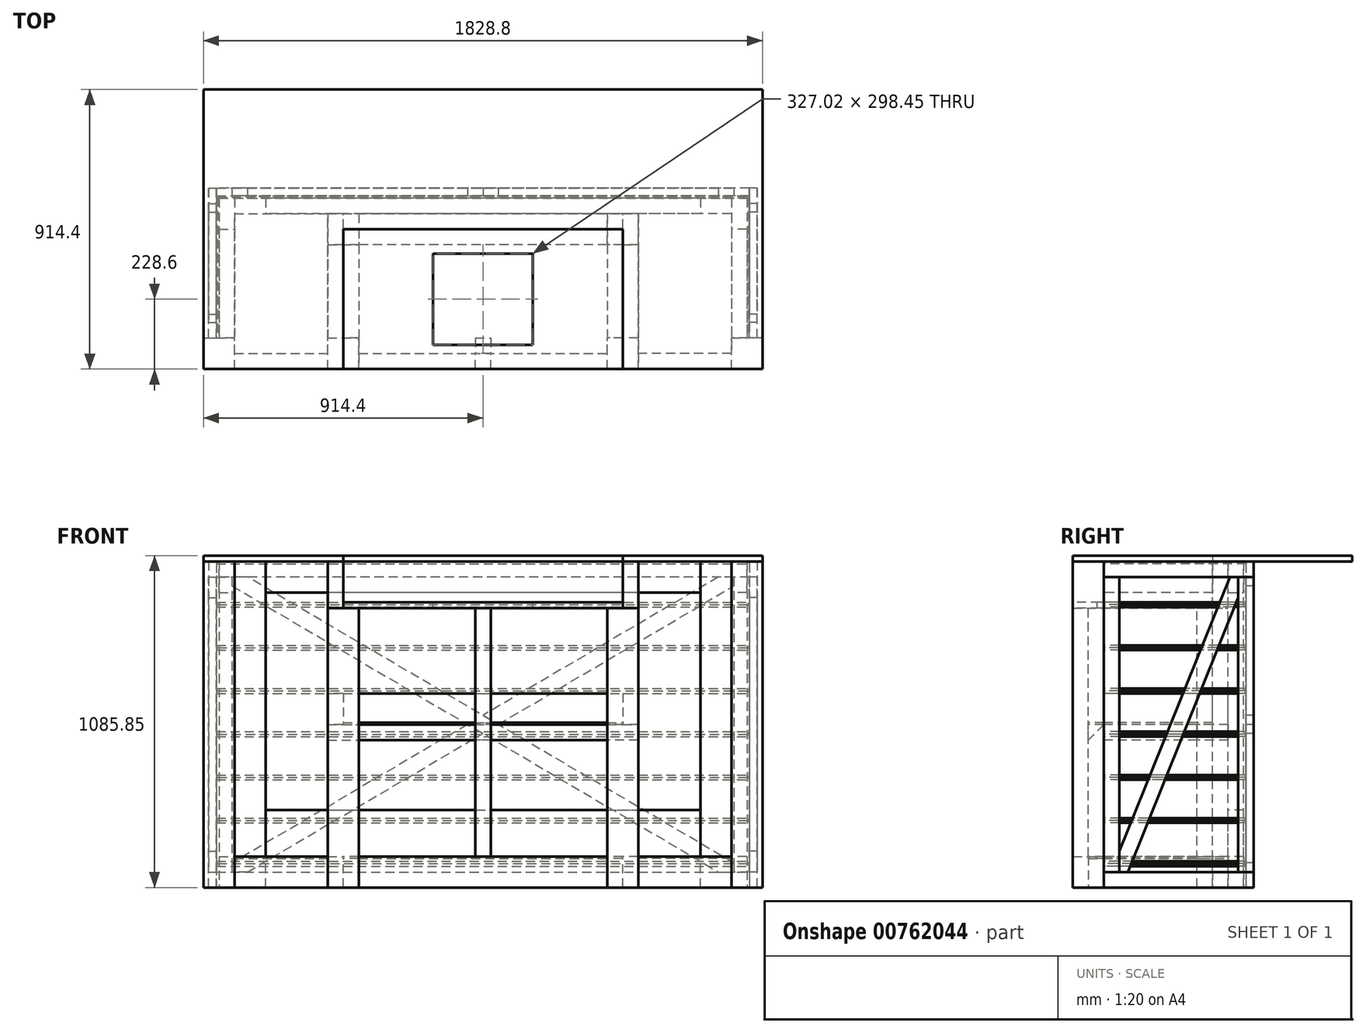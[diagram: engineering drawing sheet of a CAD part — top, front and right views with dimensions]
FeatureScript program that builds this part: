
annotation { "Feature Type Name" : "Feature", "Feature Type Description" : "" }
export const myFeature = defineFeature(function(context is Context, id is Id, definition is map)
    precondition{}
    {
        {
            var Q0;
            Q0=qCreatedBy(makeId("Top.planeOp"),FACE);
            var sketch = newSketch(context, id + "F0", { "sketchPlane" : qUnion([Q0])});
            skLineSegment(sketch, "E0.bottom", {"start": v(-914.4, -457.2) * mm, "end": v(-457.2, -457.2) * mm});
            skLineSegment(sketch, "E0.top", {"start": v(-914.4, 457.2) * mm, "end": v(914.4, 457.2) * mm});
            skLineSegment(sketch, "E0.left", {"start": v(-914.4, -457.2) * mm, "end": v(-914.4, 457.2) * mm});
            skLineSegment(sketch, "E0.right", {"start": v(914.4, -457.2) * mm, "end": v(914.4, 457.2) * mm});
            skLineSegment(sketch, "E1", {"start": v(0, 457.2) * mm, "end": v(0, -457.2) * mm, "construction": true});
            skLineSegment(sketch, "E2", {"start": v(914.4, 0) * mm, "end": v(-914.4, 0) * mm, "construction": true});
            skLineSegment(sketch, "E3.top", {"start": v(-457.2, 0) * mm, "end": v(457.2, 0) * mm});
            skLineSegment(sketch, "E3.left", {"start": v(-457.2, -457.2) * mm, "end": v(-457.2, 0) * mm});
            skLineSegment(sketch, "E3.right", {"start": v(457.2, -457.2) * mm, "end": v(457.2, 0) * mm});
            skLineSegment(sketch, "E4.trimOffspring", {"start": v(457.2, -457.2) * mm, "end": v(914.4, -457.2) * mm});
            skSolve(sketch);
        }
        {
            var Q0;
            Q0 = qSketchRegion(id + "F0", true);
            extrude(context, id + "F1", {"entities" : qUnion([Q0]), "depth" : 19.05 * mm, "offsetDistance" : 25.4 * mm});
        }
        {
            var Q0;
            Q0=makeQuery(id+"F1.opExtrude","CAP_FACE",FACE,{"disambiguationData":[OSD([sQuery(id+"F0.wireOp",EDGE,"E0.bottom"),sQuery(id+"F0.wireOp",EDGE,"E0.top"),sQuery(id+"F0.wireOp",EDGE,"E0.left"),sQuery(id+"F0.wireOp",EDGE,"E0.right"),sQuery(id+"F0.wireOp",EDGE,"E3.top"),sQuery(id+"F0.wireOp",EDGE,"E3.left"),sQuery(id+"F0.wireOp",EDGE,"E3.right"),sQuery(id+"F0.wireOp",EDGE,"E4.trimOffspring")])],"isStart":true});
            var sketch = newSketch(context, id + "F2", { "sketchPlane" : qUnion([Q0])});
            skLineSegment(sketch, "E5.bottom", {"start": v(-457.2, 0) * mm, "end": v(457.2, 0) * mm});
            skLineSegment(sketch, "E5.top", {"start": v(-457.2, -50.8) * mm, "end": v(457.2, -50.8) * mm});
            skLineSegment(sketch, "E5.left", {"start": v(-457.2, 0) * mm, "end": v(-457.2, -50.8) * mm});
            skLineSegment(sketch, "E5.right", {"start": v(457.2, 0) * mm, "end": v(457.2, -50.8) * mm});
            skSolve(sketch);
        }
        {
            var Q0;
            Q0 = qSketchRegion(id + "F2", true);
            extrude(context, id + "F3", {"entities" : qUnion([Q0]), "depth" : 152.4 * mm, "offsetDistance" : 25.4 * mm});
        }
        {
            var Q0;
            Q0=makeQuery(id+"F1.opExtrude","CAP_FACE",FACE,{"disambiguationData":[OSD([sQuery(id+"F0.wireOp",EDGE,"E0.bottom"),sQuery(id+"F0.wireOp",EDGE,"E0.top"),sQuery(id+"F0.wireOp",EDGE,"E0.left"),sQuery(id+"F0.wireOp",EDGE,"E0.right"),sQuery(id+"F0.wireOp",EDGE,"E3.top"),sQuery(id+"F0.wireOp",EDGE,"E3.left"),sQuery(id+"F0.wireOp",EDGE,"E3.right"),sQuery(id+"F0.wireOp",EDGE,"E4.trimOffspring")])],"isStart":true});
            var sketch = newSketch(context, id + "F4", { "sketchPlane" : qUnion([Q0])});
            skLineSegment(sketch, "E6.bottom", {"start": v(-914.4, 457.2) * mm, "end": v(-812.8, 457.2) * mm});
            skLineSegment(sketch, "E6.top", {"start": v(-914.4, 355.6) * mm, "end": v(-812.8, 355.6) * mm});
            skLineSegment(sketch, "E6.left", {"start": v(-914.4, 457.2) * mm, "end": v(-914.4, 355.6) * mm});
            skLineSegment(sketch, "E6.right", {"start": v(-812.8, 457.2) * mm, "end": v(-812.8, 355.6) * mm});
            skLineSegment(sketch, "E7", {"start": v(0, 0) * mm, "end": v(0, 457.2) * mm, "construction": true});
            skLineSegment(sketch, "E8.MirrorCS", {"start": v(914.4, 457.2) * mm, "end": v(812.8, 457.2) * mm});
            skLineSegment(sketch, "E9.MirrorCS", {"start": v(914.4, 355.6) * mm, "end": v(812.8, 355.6) * mm});
            skLineSegment(sketch, "E10.MirrorCS", {"start": v(812.8, 457.2) * mm, "end": v(812.8, 355.6) * mm});
            skLineSegment(sketch, "E11.MirrorCS", {"start": v(914.4, 457.2) * mm, "end": v(914.4, 355.6) * mm});
            skSolve(sketch);
        }
        {
            var Q0;
            Q0 = qSketchRegion(id + "F4", true);
            extrude(context, id + "F5", {"entities" : qUnion([Q0]), "depth" : 1066.8 * mm, "offsetDistance" : 25.4 * mm});
        }
        {
            var Q0;
            Q0=makeQuery(id+"F1.opExtrude","CAP_FACE",FACE,{"disambiguationData":[OSD([sQuery(id+"F0.wireOp",EDGE,"E0.bottom"),sQuery(id+"F0.wireOp",EDGE,"E0.top"),sQuery(id+"F0.wireOp",EDGE,"E0.left"),sQuery(id+"F0.wireOp",EDGE,"E0.right"),sQuery(id+"F0.wireOp",EDGE,"E3.top"),sQuery(id+"F0.wireOp",EDGE,"E3.left"),sQuery(id+"F0.wireOp",EDGE,"E3.right"),sQuery(id+"F0.wireOp",EDGE,"E4.trimOffspring")])],"isStart":true});
            var sketch = newSketch(context, id + "F6", { "sketchPlane" : qUnion([Q0])});
            skLineSegment(sketch, "E12.bottom", {"start": v(-457.2, 457.2) * mm, "end": v(-508, 457.2) * mm});
            skLineSegment(sketch, "E12.top", {"start": v(-457.2, -50.8) * mm, "end": v(-508, -50.8) * mm});
            skLineSegment(sketch, "E12.left", {"start": v(-457.2, 457.2) * mm, "end": v(-457.2, -50.8) * mm});
            skLineSegment(sketch, "E12.right", {"start": v(-508, 457.2) * mm, "end": v(-508, -50.8) * mm});
            skLineSegment(sketch, "E13", {"start": v(0, 0) * mm, "end": v(0, 457.2) * mm, "construction": true});
            skLineSegment(sketch, "E14.MirrorCS", {"start": v(457.2, 457.2) * mm, "end": v(508, 457.2) * mm});
            skLineSegment(sketch, "E15.MirrorCS", {"start": v(457.2, -50.8) * mm, "end": v(508, -50.8) * mm});
            skLineSegment(sketch, "E16.MirrorCS", {"start": v(457.2, 457.2) * mm, "end": v(457.2, -50.8) * mm});
            skLineSegment(sketch, "E17.MirrorCS", {"start": v(508, 457.2) * mm, "end": v(508, -50.8) * mm});
            skSolve(sketch);
        }
        {
            var Q0;
            Q0 = qSketchRegion(id + "F6", true);
            extrude(context, id + "F7", {"entities" : qUnion([Q0]), "depth" : 152.4 * mm, "offsetDistance" : 25.4 * mm});
        }
        {
            var Q0;
            Q0=makeQuery(id+"F3.opExtrude","CAP_FACE",FACE,{"disambiguationData":[OSD([sQuery(id+"F2.wireOp",EDGE,"E5.bottom"),sQuery(id+"F2.wireOp",EDGE,"E5.top"),sQuery(id+"F2.wireOp",EDGE,"E5.left"),sQuery(id+"F2.wireOp",EDGE,"E5.right")])],"isStart":false});
            var sketch = newSketch(context, id + "F8", { "sketchPlane" : qUnion([Q0])});
            skLineSegment(sketch, "E18.bottom", {"start": v(-457.2, 0) * mm, "end": v(457.2, 0) * mm});
            skLineSegment(sketch, "E18.top", {"start": v(-457.2, 457.2) * mm, "end": v(457.2, 457.2) * mm});
            skLineSegment(sketch, "E18.left", {"start": v(-457.2, 0) * mm, "end": v(-457.2, 457.2) * mm});
            skLineSegment(sketch, "E18.right", {"start": v(457.2, 0) * mm, "end": v(457.2, 457.2) * mm});
            skSolve(sketch);
        }
        {
            var Q0;
            Q0 = qSketchRegion(id + "F8", true);
            extrude(context, id + "F9", {"entities" : qUnion([Q0]), "oppositeDirection" : true, "depth" : 19.05 * mm, "offsetDistance" : 25.4 * mm});
        }
        {
            var Q0;
            Q0=makeQuery(id+"F9.opExtrude","CAP_FACE",FACE,{"disambiguationData":[OSD([sQuery(id+"F8.wireOp",EDGE,"E18.bottom"),sQuery(id+"F8.wireOp",EDGE,"E18.top"),sQuery(id+"F8.wireOp",EDGE,"E18.left"),sQuery(id+"F8.wireOp",EDGE,"E18.right")])],"isStart":false});
            var sketch = newSketch(context, id + "F10", { "sketchPlane" : qUnion([Q0])});
            skLineSegment(sketch, "E19", {"start": v(0, 0) * mm, "end": v(0, -457.2) * mm, "construction": true});
            skLineSegment(sketch, "E20.bottom", {"start": v(163.51, -79.37) * mm, "end": v(-163.51, -79.37) * mm});
            skLineSegment(sketch, "E20.top", {"start": v(163.51, -377.82) * mm, "end": v(-163.51, -377.82) * mm});
            skLineSegment(sketch, "E20.left", {"start": v(163.51, -79.37) * mm, "end": v(163.51, -377.82) * mm});
            skLineSegment(sketch, "E20.right", {"start": v(-163.51, -79.37) * mm, "end": v(-163.51, -377.82) * mm});
            skPoint(sketch, "E20.middle", {"position": v(0, -228.6) * mm});
            skSolve(sketch);
        }
        {
            var Q0;
            Q0=makeQuery(id+"F10.imprint","IMPRINT",FACE,{"disambiguationData":[TD([[makeQuery(id+"F10.imprint","IMPRINT",EDGE,{"derivedFrom":sQuery(id+"F10.wireOp",EDGE,"E20.bottom")}),1.0]])]});
            extrude(context, id + "F11", {"entities" : qUnion([Q0]), "operationType" : NewBodyOperationType.REMOVE, "endBound" : BoundingType.UP_TO_NEXT, "oppositeDirection" : true, "depth" : 34.92 * mm, "offsetDistance" : 25.4 * mm});
        }
        {
            var Q0;
            Q0=makeQuery(id+"F7.opExtrude","CAP_FACE",FACE,{"disambiguationData":[OSD([sQuery(id+"F6.wireOp",EDGE,"E12.bottom"),sQuery(id+"F6.wireOp",EDGE,"E12.top"),sQuery(id+"F6.wireOp",EDGE,"E12.left"),sQuery(id+"F6.wireOp",EDGE,"E12.right")])],"isStart":false});
            var sketch = newSketch(context, id + "F12", { "sketchPlane" : qUnion([Q0])});
            skLineSegment(sketch, "E21.bottom", {"start": v(-508, 457.2) * mm, "end": v(-406.4, 457.2) * mm});
            skLineSegment(sketch, "E21.top", {"start": v(-508, 355.6) * mm, "end": v(-406.4, 355.6) * mm});
            skLineSegment(sketch, "E21.left", {"start": v(-508, 457.2) * mm, "end": v(-508, 355.6) * mm});
            skLineSegment(sketch, "E21.right", {"start": v(-406.4, 457.2) * mm, "end": v(-406.4, 355.6) * mm});
            skLineSegment(sketch, "E22", {"start": v(0, 0) * mm, "end": v(0, 457.2) * mm, "construction": true});
            skLineSegment(sketch, "E23.MirrorCS", {"start": v(508, 457.2) * mm, "end": v(406.4, 457.2) * mm});
            skLineSegment(sketch, "E24.MirrorCS", {"start": v(508, 355.6) * mm, "end": v(406.4, 355.6) * mm});
            skLineSegment(sketch, "E25.MirrorCS", {"start": v(406.4, 457.2) * mm, "end": v(406.4, 355.6) * mm});
            skLineSegment(sketch, "E26.MirrorCS", {"start": v(508, 457.2) * mm, "end": v(508, 355.6) * mm});
            skSolve(sketch);
        }
        {
            var Q0;
            Q0 = qSketchRegion(id + "F12", true);
            var Q1;
            Q1=makeQuery(id+"F5.opExtrude","CAP_FACE",FACE,{"disambiguationData":[OSD([sQuery(id+"F4.wireOp",EDGE,"E6.bottom"),sQuery(id+"F4.wireOp",EDGE,"E6.top"),sQuery(id+"F4.wireOp",EDGE,"E6.left"),sQuery(id+"F4.wireOp",EDGE,"E6.right")])],"isStart":false});
            extrude(context, id + "F13", {"entities" : qUnion([Q0]), "endBound" : BoundingType.UP_TO_SURFACE, "depth" : 25.4 * mm, "endBoundEntityFace" : qUnion([Q1]), "offsetDistance" : 25.4 * mm});
        }
        {
            var Q0;
            Q0=makeQuery(id+"F9.opExtrude","CAP_FACE",FACE,{"disambiguationData":[OSD([sQuery(id+"F8.wireOp",EDGE,"E18.bottom"),sQuery(id+"F8.wireOp",EDGE,"E18.top"),sQuery(id+"F8.wireOp",EDGE,"E18.left"),sQuery(id+"F8.wireOp",EDGE,"E18.right")])],"isStart":true});
            var sketch = newSketch(context, id + "F14", { "sketchPlane" : qUnion([Q0])});
            skLineSegment(sketch, "E27", {"start": v(0, 0) * mm, "end": v(0, 457.2) * mm, "construction": true});
            skLineSegment(sketch, "E28.bottom", {"start": v(25.4, 457.2) * mm, "end": v(-25.4, 457.2) * mm});
            skLineSegment(sketch, "E28.top", {"start": v(25.4, 406.4) * mm, "end": v(-25.4, 406.4) * mm});
            skLineSegment(sketch, "E28.left", {"start": v(25.4, 457.2) * mm, "end": v(25.4, 406.4) * mm});
            skLineSegment(sketch, "E28.right", {"start": v(-25.4, 457.2) * mm, "end": v(-25.4, 406.4) * mm});
            skSolve(sketch);
        }
        {
            var Q0;
            Q0 = qSketchRegion(id + "F14", true);
            var Q1;
            Q1=makeQuery(id+"F13.opExtrude","CAP_FACE",FACE,{"disambiguationData":[OSD([sQuery(id+"F12.wireOp",EDGE,"E21.bottom"),sQuery(id+"F12.wireOp",EDGE,"E21.top"),sQuery(id+"F12.wireOp",EDGE,"E21.left"),sQuery(id+"F12.wireOp",EDGE,"E21.right")])],"isStart":false});
            extrude(context, id + "F15", {"entities" : qUnion([Q0]), "depth" : 812.8 * mm, "endBoundEntityFace" : qUnion([Q1]), "offsetDistance" : 25.4 * mm});
        }
        {
            var Q0;
            Q0=makeQuery(id+"F7.opExtrude","CAP_FACE",FACE,{"disambiguationData":[OSD([sQuery(id+"F6.wireOp",EDGE,"E14.MirrorCS"),sQuery(id+"F6.wireOp",EDGE,"E15.MirrorCS"),sQuery(id+"F6.wireOp",EDGE,"E16.MirrorCS"),sQuery(id+"F6.wireOp",EDGE,"E17.MirrorCS")])],"isStart":false});
            var sketch = newSketch(context, id + "F16", { "sketchPlane" : qUnion([Q0])});
            skLineSegment(sketch, "E29.bottom", {"start": v(508, -50.8) * mm, "end": v(406.4, -50.8) * mm});
            skLineSegment(sketch, "E29.top", {"start": v(508, 50.8) * mm, "end": v(406.4, 50.8) * mm});
            skLineSegment(sketch, "E29.left", {"start": v(508, -50.8) * mm, "end": v(508, 50.8) * mm});
            skLineSegment(sketch, "E29.right", {"start": v(406.4, -50.8) * mm, "end": v(406.4, 50.8) * mm});
            skLineSegment(sketch, "E30", {"start": v(0, 0) * mm, "end": v(0, 457.2) * mm, "construction": true});
            skLineSegment(sketch, "E31.MirrorCS", {"start": v(-508, -50.8) * mm, "end": v(-406.4, -50.8) * mm});
            skLineSegment(sketch, "E32.MirrorCS", {"start": v(-508, 50.8) * mm, "end": v(-406.4, 50.8) * mm});
            skLineSegment(sketch, "E33.MirrorCS", {"start": v(-406.4, -50.8) * mm, "end": v(-406.4, 50.8) * mm});
            skLineSegment(sketch, "E34.MirrorCS", {"start": v(-508, -50.8) * mm, "end": v(-508, 50.8) * mm});
            skSolve(sketch);
        }
        {
            var Q0;
            Q0 = qSketchRegion(id + "F16", true);
            var Q1;
            Q1=makeQuery(id+"F13.opExtrude","CAP_FACE",FACE,{"disambiguationData":[OSD([sQuery(id+"F12.wireOp",EDGE,"E23.MirrorCS"),sQuery(id+"F12.wireOp",EDGE,"E24.MirrorCS"),sQuery(id+"F12.wireOp",EDGE,"E25.MirrorCS"),sQuery(id+"F12.wireOp",EDGE,"E26.MirrorCS")])],"isStart":false});
            extrude(context, id + "F17", {"entities" : qUnion([Q0]), "endBound" : BoundingType.UP_TO_SURFACE, "depth" : 914.4 * mm, "endBoundEntityFace" : qUnion([Q1]), "offsetDistance" : 25.4 * mm});
        }
        {
            var Q0;
            Q0=makeQuery(id+"F13.opExtrude","SWEPT_FACE",FACE,{"disambiguationData":[OSD([sQuery(id+"F12.wireOp",EDGE,"E24.MirrorCS")])]});
            var sketch = newSketch(context, id + "F18", { "sketchPlane" : qUnion([Q0])});
            skPoint(sketch, "E35.oppositeSnap0", {"position": v(-457.2, -1066.8) * mm});
            skLineSegment(sketch, "E35.bottom", {"start": v(-508, -1066.8) * mm, "end": v(-457.2, -1066.8) * mm});
            skLineSegment(sketch, "E35.top", {"start": v(-508, -965.2) * mm, "end": v(-457.2, -965.2) * mm});
            skLineSegment(sketch, "E35.left", {"start": v(-508, -1066.8) * mm, "end": v(-508, -965.2) * mm});
            skLineSegment(sketch, "E35.right", {"start": v(-457.2, -1066.8) * mm, "end": v(-457.2, -965.2) * mm});
            skLineSegment(sketch, "E36", {"start": v(0, 0) * mm, "end": v(0, -1066.8) * mm, "construction": true});
            skPoint(sketch, "E37.MirrorP", {"position": v(457.2, -1066.8) * mm});
            skLineSegment(sketch, "E38.MirrorCS", {"start": v(508, -1066.8) * mm, "end": v(457.2, -1066.8) * mm});
            skLineSegment(sketch, "E39.MirrorCS", {"start": v(508, -965.2) * mm, "end": v(457.2, -965.2) * mm});
            skLineSegment(sketch, "E40.MirrorCS", {"start": v(457.2, -1066.8) * mm, "end": v(457.2, -965.2) * mm});
            skLineSegment(sketch, "E41.MirrorCS", {"start": v(508, -1066.8) * mm, "end": v(508, -965.2) * mm});
            skSolve(sketch);
        }
        {
            var Q0;
            Q0 = qSketchRegion(id + "F18", true);
            var Q1;
            Q1=makeQuery(id+"F17.opExtrude","SWEPT_FACE",FACE,{"disambiguationData":[OSD([sQuery(id+"F16.wireOp",EDGE,"E29.top")])]});
            extrude(context, id + "F19", {"entities" : qUnion([Q0]), "endBound" : BoundingType.UP_TO_SURFACE, "depth" : 25.4 * mm, "endBoundEntityFace" : qUnion([Q1]), "offsetDistance" : 25.4 * mm});
        }
        {
            var Q0;
            Q0=makeQuery(id+"F13.opExtrude","SWEPT_FACE",FACE,{"disambiguationData":[OSD([sQuery(id+"F12.wireOp",EDGE,"E25.MirrorCS")])]});
            var sketch = newSketch(context, id + "F20", { "sketchPlane" : qUnion([Q0])});
            skPoint(sketch, "E42.oppositeSnap0", {"position": v(406.4, -1066.8) * mm});
            skLineSegment(sketch, "E42.bottom", {"start": v(457.2, -1066.8) * mm, "end": v(406.4, -1066.8) * mm});
            skLineSegment(sketch, "E42.top", {"start": v(457.2, -965.2) * mm, "end": v(406.4, -965.2) * mm});
            skLineSegment(sketch, "E42.left", {"start": v(457.2, -1066.8) * mm, "end": v(457.2, -965.2) * mm});
            skLineSegment(sketch, "E42.right", {"start": v(406.4, -1066.8) * mm, "end": v(406.4, -965.2) * mm});
            skLineSegment(sketch, "E43", {"start": v(0, 0) * mm, "end": v(0, -1066.8) * mm, "construction": true});
            skLineSegment(sketch, "E44.bottom", {"start": v(0, -1066.8) * mm, "end": v(-50.8, -1066.8) * mm});
            skLineSegment(sketch, "E44.top", {"start": v(0, -965.2) * mm, "end": v(-50.8, -965.2) * mm});
            skLineSegment(sketch, "E44.left", {"start": v(0, -1066.8) * mm, "end": v(0, -965.2) * mm});
            skLineSegment(sketch, "E44.right", {"start": v(-50.8, -1066.8) * mm, "end": v(-50.8, -965.2) * mm});
            skSolve(sketch);
        }
        {
            var Q0;
            Q0 = qSketchRegion(id + "F20", true);
            var Q1;
            Q1=makeQuery(id+"F13.opExtrude","SWEPT_FACE",FACE,{"disambiguationData":[OSD([sQuery(id+"F12.wireOp",EDGE,"E21.right")])]});
            extrude(context, id + "F21", {"entities" : qUnion([Q0]), "endBound" : BoundingType.UP_TO_SURFACE, "depth" : 25.4 * mm, "endBoundEntityFace" : qUnion([Q1]), "offsetDistance" : 25.4 * mm});
        }
        {
            var Q0;
            Q0=makeQuery(id+"F1.opExtrude","CAP_FACE",FACE,{"disambiguationData":[OSD([sQuery(id+"F0.wireOp",EDGE,"E0.bottom"),sQuery(id+"F0.wireOp",EDGE,"E0.top"),sQuery(id+"F0.wireOp",EDGE,"E0.left"),sQuery(id+"F0.wireOp",EDGE,"E0.right"),sQuery(id+"F0.wireOp",EDGE,"E3.top"),sQuery(id+"F0.wireOp",EDGE,"E3.left"),sQuery(id+"F0.wireOp",EDGE,"E3.right"),sQuery(id+"F0.wireOp",EDGE,"E4.trimOffspring")])],"isStart":true});
            var sketch = newSketch(context, id + "F22", { "sketchPlane" : qUnion([Q0])});
            skLineSegment(sketch, "E45.bottom", {"start": v(812.8, -101.6) * mm, "end": v(711.2, -101.6) * mm});
            skLineSegment(sketch, "E45.top", {"start": v(812.8, -50.8) * mm, "end": v(711.2, -50.8) * mm});
            skLineSegment(sketch, "E45.left", {"start": v(812.8, -101.6) * mm, "end": v(812.8, -50.8) * mm});
            skLineSegment(sketch, "E45.right", {"start": v(711.2, -101.6) * mm, "end": v(711.2, -50.8) * mm});
            skLineSegment(sketch, "E46", {"start": v(0, 0) * mm, "end": v(0, -457.2) * mm, "construction": true});
            skLineSegment(sketch, "E47.MirrorCS", {"start": v(-812.8, -101.6) * mm, "end": v(-711.2, -101.6) * mm});
            skLineSegment(sketch, "E48.MirrorCS", {"start": v(-812.8, -50.8) * mm, "end": v(-711.2, -50.8) * mm});
            skLineSegment(sketch, "E49.MirrorCS", {"start": v(-711.2, -101.6) * mm, "end": v(-711.2, -50.8) * mm});
            skLineSegment(sketch, "E50.MirrorCS", {"start": v(-812.8, -101.6) * mm, "end": v(-812.8, -50.8) * mm});
            skSolve(sketch);
        }
        {
            var Q0;
            Q0 = qSketchRegion(id + "F22", true);
            var Q1;
            Q1=makeQuery(id+"F5.opExtrude","CAP_FACE",FACE,{"disambiguationData":[OSD([sQuery(id+"F4.wireOp",EDGE,"E6.bottom"),sQuery(id+"F4.wireOp",EDGE,"E6.top"),sQuery(id+"F4.wireOp",EDGE,"E6.left"),sQuery(id+"F4.wireOp",EDGE,"E6.right")])],"isStart":false});
            extrude(context, id + "F23", {"entities" : qUnion([Q0]), "endBound" : BoundingType.UP_TO_SURFACE, "depth" : 25.4 * mm, "endBoundEntityFace" : qUnion([Q1]), "offsetDistance" : 25.4 * mm});
        }
        {
            var Q0;
            Q0=makeQuery(id+"F1.opExtrude","CAP_FACE",FACE,{"disambiguationData":[OSD([sQuery(id+"F0.wireOp",EDGE,"E0.bottom"),sQuery(id+"F0.wireOp",EDGE,"E0.top"),sQuery(id+"F0.wireOp",EDGE,"E0.left"),sQuery(id+"F0.wireOp",EDGE,"E0.right"),sQuery(id+"F0.wireOp",EDGE,"E3.top"),sQuery(id+"F0.wireOp",EDGE,"E3.left"),sQuery(id+"F0.wireOp",EDGE,"E3.right"),sQuery(id+"F0.wireOp",EDGE,"E4.trimOffspring")])],"isStart":true});
            var sketch = newSketch(context, id + "F24", { "sketchPlane" : qUnion([Q0])});
            skLineSegment(sketch, "E51", {"start": v(0, 0) * mm, "end": v(0, 457.2) * mm, "construction": true});
            skLineSegment(sketch, "E52.bottom", {"start": v(863.6, -101.6) * mm, "end": v(812.8, -101.6) * mm});
            skLineSegment(sketch, "E52.top", {"start": v(863.6, 0) * mm, "end": v(812.8, 0) * mm});
            skLineSegment(sketch, "E52.left", {"start": v(863.6, -101.6) * mm, "end": v(863.6, 0) * mm});
            skLineSegment(sketch, "E52.right", {"start": v(812.8, -101.6) * mm, "end": v(812.8, 0) * mm});
            skLineSegment(sketch, "E53.MirrorCS", {"start": v(-812.8, -101.6) * mm, "end": v(-812.8, 0) * mm});
            skLineSegment(sketch, "E54.MirrorCS", {"start": v(-863.6, 0) * mm, "end": v(-812.8, 0) * mm});
            skLineSegment(sketch, "E55.MirrorCS", {"start": v(-863.6, -101.6) * mm, "end": v(-863.6, 0) * mm});
            skLineSegment(sketch, "E56.MirrorCS", {"start": v(-863.6, -101.6) * mm, "end": v(-812.8, -101.6) * mm});
            skSolve(sketch);
        }
        {
            var Q0;
            Q0 = qSketchRegion(id + "F24", true);
            var Q1;
            Q1=makeQuery(id+"F5.opExtrude","CAP_FACE",FACE,{"disambiguationData":[OSD([sQuery(id+"F4.wireOp",EDGE,"E6.bottom"),sQuery(id+"F4.wireOp",EDGE,"E6.top"),sQuery(id+"F4.wireOp",EDGE,"E6.left"),sQuery(id+"F4.wireOp",EDGE,"E6.right")])],"isStart":false});
            extrude(context, id + "F25", {"entities" : qUnion([Q0]), "endBound" : BoundingType.UP_TO_SURFACE, "depth" : 25.4 * mm, "endBoundEntityFace" : qUnion([Q1]), "offsetDistance" : 25.4 * mm});
        }
        {
            var Q0;
            Q0=makeQuery(id+"F5.opExtrude","SWEPT_FACE",FACE,{"disambiguationData":[OSD([sQuery(id+"F4.wireOp",EDGE,"E6.top")])]});
            var sketch = newSketch(context, id + "F26", { "sketchPlane" : qUnion([Q0])});
            skLineSegment(sketch, "E57", {"start": v(0, 0) * mm, "end": v(0, -1066.8) * mm, "construction": true});
            skPoint(sketch, "E58.oppositeSnap0", {"position": v(863.6, 0) * mm});
            skPoint(sketch, "E59.oppositeSnap0", {"position": v(863.6, -1066.8) * mm});
            skLineSegment(sketch, "E59.bottom", {"start": v(812.8, -1066.8) * mm, "end": v(863.6, -1066.8) * mm});
            skLineSegment(sketch, "E59.top", {"start": v(812.8, -965.2) * mm, "end": v(863.6, -965.2) * mm});
            skLineSegment(sketch, "E59.left", {"start": v(812.8, -1066.8) * mm, "end": v(812.8, -965.2) * mm});
            skLineSegment(sketch, "E59.right", {"start": v(863.6, -1066.8) * mm, "end": v(863.6, -965.2) * mm});
            skLineSegment(sketch, "E60.bottom", {"start": v(812.8, 0) * mm, "end": v(863.6, 0) * mm});
            skLineSegment(sketch, "E60.top", {"start": v(812.8, -101.6) * mm, "end": v(863.6, -101.6) * mm});
            skLineSegment(sketch, "E60.left", {"start": v(812.8, 0) * mm, "end": v(812.8, -101.6) * mm});
            skLineSegment(sketch, "E60.right", {"start": v(863.6, 0) * mm, "end": v(863.6, -101.6) * mm});
            skLineSegment(sketch, "E61.MirrorCS", {"start": v(-812.8, 0) * mm, "end": v(-863.6, 0) * mm});
            skLineSegment(sketch, "E62.MirrorCS", {"start": v(-812.8, -1066.8) * mm, "end": v(-812.8, -965.2) * mm});
            skLineSegment(sketch, "E63.MirrorCS", {"start": v(-812.8, -965.2) * mm, "end": v(-863.6, -965.2) * mm});
            skLineSegment(sketch, "E64.MirrorCS", {"start": v(-863.6, 0) * mm, "end": v(-863.6, -101.6) * mm});
            skLineSegment(sketch, "E65.MirrorCS", {"start": v(-812.8, 0) * mm, "end": v(-812.8, -101.6) * mm});
            skLineSegment(sketch, "E66.MirrorCS", {"start": v(-812.8, -101.6) * mm, "end": v(-863.6, -101.6) * mm});
            skLineSegment(sketch, "E67.MirrorCS", {"start": v(-812.8, -1066.8) * mm, "end": v(-863.6, -1066.8) * mm});
            skLineSegment(sketch, "E68.MirrorCS", {"start": v(-863.6, -1066.8) * mm, "end": v(-863.6, -965.2) * mm});
            skPoint(sketch, "E69.MirrorP", {"position": v(-863.6, -1066.8) * mm});
            skPoint(sketch, "E70.MirrorP", {"position": v(-863.6, 0) * mm});
            skSolve(sketch);
        }
        {
            var Q0;
            Q0 = qSketchRegion(id + "F26", true);
            var Q1;
            Q1=makeQuery(id+"F25.opExtrude","SWEPT_FACE",FACE,{"disambiguationData":[OSD([sQuery(id+"F24.wireOp",EDGE,"E54.MirrorCS")])]});
            extrude(context, id + "F27", {"entities" : qUnion([Q0]), "endBound" : BoundingType.UP_TO_SURFACE, "depth" : 25.4 * mm, "endBoundEntityFace" : qUnion([Q1]), "offsetDistance" : 25.4 * mm});
        }
        {
            var Q0;
            Q0=makeQuery(id+"F23.opExtrude","SWEPT_FACE",FACE,{"disambiguationData":[OSD([sQuery(id+"F22.wireOp",EDGE,"E49.MirrorCS")])]});
            var sketch = newSketch(context, id + "F28", { "sketchPlane" : qUnion([Q0])});
            skLineSegment(sketch, "E71.bottom", {"start": v(101.6, 0) * mm, "end": v(50.8, 0) * mm});
            skLineSegment(sketch, "E71.top", {"start": v(101.6, -101.6) * mm, "end": v(50.8, -101.6) * mm});
            skLineSegment(sketch, "E71.left", {"start": v(101.6, 0) * mm, "end": v(101.6, -101.6) * mm});
            skLineSegment(sketch, "E71.right", {"start": v(50.8, 0) * mm, "end": v(50.8, -101.6) * mm});
            skLineSegment(sketch, "E72.bottom", {"start": v(101.6, -1066.8) * mm, "end": v(50.8, -1066.8) * mm});
            skLineSegment(sketch, "E72.top", {"start": v(101.6, -965.2) * mm, "end": v(50.8, -965.2) * mm});
            skLineSegment(sketch, "E72.left", {"start": v(101.6, -1066.8) * mm, "end": v(101.6, -965.2) * mm});
            skLineSegment(sketch, "E72.right", {"start": v(50.8, -1066.8) * mm, "end": v(50.8, -965.2) * mm});
            skSolve(sketch);
        }
        {
            var Q0;
            Q0 = qSketchRegion(id + "F28", true);
            var Q1;
            Q1=makeQuery(id+"F23.opExtrude","SWEPT_FACE",FACE,{"disambiguationData":[OSD([sQuery(id+"F22.wireOp",EDGE,"E45.right")])]});
            extrude(context, id + "F29", {"entities" : qUnion([Q0]), "endBound" : BoundingType.UP_TO_SURFACE, "depth" : 25.4 * mm, "endBoundEntityFace" : qUnion([Q1]), "offsetDistance" : 25.4 * mm});
        }
        {
            var Q0;
            Q0=makeQuery(id+"F5.opExtrude","SWEPT_FACE",FACE,{"disambiguationData":[OSD([sQuery(id+"F4.wireOp",EDGE,"E10.MirrorCS")])]});
            var sketch = newSketch(context, id + "F30", { "sketchPlane" : qUnion([Q0])});
            skLineSegment(sketch, "E73.bottom", {"start": v(457.2, -1066.8) * mm, "end": v(406.4, -1066.8) * mm});
            skLineSegment(sketch, "E73.top", {"start": v(457.2, -965.2) * mm, "end": v(406.4, -965.2) * mm});
            skLineSegment(sketch, "E73.left", {"start": v(457.2, -1066.8) * mm, "end": v(457.2, -965.2) * mm});
            skLineSegment(sketch, "E73.right", {"start": v(406.4, -1066.8) * mm, "end": v(406.4, -965.2) * mm});
            skSolve(sketch);
        }
        {
            var Q0;
            Q0 = qSketchRegion(id + "F30", true);
            var Q1;
            Q1=makeQuery(id+"F13.opExtrude","SWEPT_FACE",FACE,{"disambiguationData":[OSD([sQuery(id+"F12.wireOp",EDGE,"E26.MirrorCS")])]});
            extrude(context, id + "F31", {"entities" : qUnion([Q0]), "endBound" : BoundingType.UP_TO_SURFACE, "depth" : 25.4 * mm, "endBoundEntityFace" : qUnion([Q1]), "offsetDistance" : 25.4 * mm});
        }
        {
            var Q0;
            Q0=makeQuery(id+"F5.opExtrude","SWEPT_FACE",FACE,{"disambiguationData":[OSD([sQuery(id+"F4.wireOp",EDGE,"E6.right")])]});
            var sketch = newSketch(context, id + "F32", { "sketchPlane" : qUnion([Q0])});
            skPoint(sketch, "E74.oppositeSnap0", {"position": v(-406.4, -1066.8) * mm});
            skLineSegment(sketch, "E74.bottom", {"start": v(-457.2, -1066.8) * mm, "end": v(-406.4, -1066.8) * mm});
            skLineSegment(sketch, "E74.top", {"start": v(-457.2, -965.2) * mm, "end": v(-406.4, -965.2) * mm});
            skLineSegment(sketch, "E74.left", {"start": v(-457.2, -1066.8) * mm, "end": v(-457.2, -965.2) * mm});
            skLineSegment(sketch, "E74.right", {"start": v(-406.4, -1066.8) * mm, "end": v(-406.4, -965.2) * mm});
            skSolve(sketch);
        }
        {
            var Q0;
            Q0 = qSketchRegion(id + "F32", true);
            var Q1;
            Q1=makeQuery(id+"F13.opExtrude","SWEPT_FACE",FACE,{"disambiguationData":[OSD([sQuery(id+"F12.wireOp",EDGE,"E21.left")])]});
            extrude(context, id + "F33", {"entities" : qUnion([Q0]), "endBound" : BoundingType.UP_TO_SURFACE, "depth" : 25.4 * mm, "endBoundEntityFace" : qUnion([Q1]), "offsetDistance" : 25.4 * mm});
        }
        {
            var Q0;
            Q0=makeQuery(id+"F23.opExtrude","SWEPT_FACE",FACE,{"disambiguationData":[OSD([sQuery(id+"F22.wireOp",EDGE,"E45.right")])]});
            var sketch = newSketch(context, id + "F34", { "sketchPlane" : qUnion([Q0])});
            skLineSegment(sketch, "E75.bottom", {"start": v(-101.6, -965.2) * mm, "end": v(-50.8, -965.2) * mm});
            skLineSegment(sketch, "E75.top", {"start": v(-101.6, -812.8) * mm, "end": v(-50.8, -812.8) * mm});
            skLineSegment(sketch, "E75.left", {"start": v(-101.6, -965.2) * mm, "end": v(-101.6, -812.8) * mm});
            skLineSegment(sketch, "E75.right", {"start": v(-50.8, -965.2) * mm, "end": v(-50.8, -812.8) * mm});
            skSolve(sketch);
        }
        {
            var Q0;
            Q0 = qSketchRegion(id + "F34", true);
            var Q1;
            Q1=makeQuery(id+"F23.opExtrude","SWEPT_FACE",FACE,{"disambiguationData":[OSD([sQuery(id+"F22.wireOp",EDGE,"E49.MirrorCS")])]});
            extrude(context, id + "F35", {"entities" : qUnion([Q0]), "endBound" : BoundingType.UP_TO_SURFACE, "depth" : 25.4 * mm, "endBoundEntityFace" : qUnion([Q1]), "offsetDistance" : 25.4 * mm});
        }
        {
            var Q0;
            Q0=makeQuery(id+"F21.opExtrude","SWEPT_FACE",FACE,{"disambiguationData":[OSD([sQuery(id+"F20.wireOp",EDGE,"E44.top")])]});
            var sketch = newSketch(context, id + "F36", { "sketchPlane" : qUnion([Q0])});
            skPoint(sketch, "E76.0", {"position": v(406.4, -50.8) * mm});
            skPoint(sketch, "E77.0", {"position": v(457.2, -50.8) * mm});
            skPoint(sketch, "E78.0", {"position": v(406.4, 0) * mm});
            skPoint(sketch, "E79.0", {"position": v(-406.4, 0) * mm});
            skPoint(sketch, "E80.0", {"position": v(-406.4, -50.8) * mm});
            skPoint(sketch, "E81.0", {"position": v(-457.2, -50.8) * mm});
            skPoint(sketch, "E82.0", {"position": v(-406.4, -406.4) * mm});
            skPoint(sketch, "E83.0", {"position": v(-406.4, -355.6) * mm});
            skPoint(sketch, "E84.0", {"position": v(-457.2, -355.6) * mm});
            skPoint(sketch, "E85.0", {"position": v(406.4, -406.4) * mm});
            skPoint(sketch, "E86.0", {"position": v(406.4, -355.6) * mm});
            skPoint(sketch, "E87.0", {"position": v(457.2, -355.6) * mm});
            skLineSegment(sketch, "E88", {"start": v(-457.2, -50.8) * mm, "end": v(-457.2, -355.6) * mm});
            skLineSegment(sketch, "E89", {"start": v(-406.4, -355.6) * mm, "end": v(-406.4, -406.4) * mm});
            skLineSegment(sketch, "E90", {"start": v(406.4, -406.4) * mm, "end": v(406.4, -355.6) * mm});
            skLineSegment(sketch, "E91", {"start": v(457.2, -355.6) * mm, "end": v(457.2, -50.8) * mm});
            skLineSegment(sketch, "E92", {"start": v(406.4, -50.8) * mm, "end": v(406.4, 0) * mm});
            skLineSegment(sketch, "E93", {"start": v(-406.4, 0) * mm, "end": v(-406.4, -50.8) * mm});
            skLineSegment(sketch, "E94", {"start": v(-406.4, -355.6) * mm, "end": v(-457.2, -355.6) * mm});
            skLineSegment(sketch, "E95", {"start": v(457.2, -355.6) * mm, "end": v(406.4, -355.6) * mm});
            skLineSegment(sketch, "E96", {"start": v(406.4, -406.4) * mm, "end": v(-406.4, -406.4) * mm});
            skLineSegment(sketch, "E97", {"start": v(457.2, -50.8) * mm, "end": v(406.4, -50.8) * mm});
            skLineSegment(sketch, "E98", {"start": v(406.4, 0) * mm, "end": v(-406.4, 0) * mm});
            skLineSegment(sketch, "E99", {"start": v(-406.4, -50.8) * mm, "end": v(-457.2, -50.8) * mm});
            skPoint(sketch, "E100.0", {"position": v(-812.8, 50.8) * mm});
            skPoint(sketch, "E101.0", {"position": v(-508, 50.8) * mm});
            skPoint(sketch, "E102.0", {"position": v(-508, -406.4) * mm});
            skPoint(sketch, "E103.0", {"position": v(-812.8, -406.4) * mm});
            skPoint(sketch, "E104.0", {"position": v(508, -406.4) * mm});
            skPoint(sketch, "E105.0", {"position": v(812.8, 50.8) * mm});
            skPoint(sketch, "E106.0", {"position": v(508, 50.8) * mm});
            skPoint(sketch, "E107.0", {"position": v(812.8, -406.4) * mm});
            skLineSegment(sketch, "E108.bottom", {"start": v(-812.8, -406.4) * mm, "end": v(-508, -406.4) * mm});
            skLineSegment(sketch, "E108.top", {"start": v(-812.8, 50.8) * mm, "end": v(-508, 50.8) * mm});
            skLineSegment(sketch, "E108.left", {"start": v(-812.8, -406.4) * mm, "end": v(-812.8, 50.8) * mm});
            skLineSegment(sketch, "E108.right", {"start": v(-508, -406.4) * mm, "end": v(-508, 50.8) * mm});
            skLineSegment(sketch, "E109.bottom", {"start": v(812.8, 50.8) * mm, "end": v(508, 50.8) * mm});
            skLineSegment(sketch, "E109.top", {"start": v(812.8, -406.4) * mm, "end": v(508, -406.4) * mm});
            skLineSegment(sketch, "E109.left", {"start": v(812.8, 50.8) * mm, "end": v(812.8, -406.4) * mm});
            skLineSegment(sketch, "E109.right", {"start": v(508, 50.8) * mm, "end": v(508, -406.4) * mm});
            skSolve(sketch);
        }
        {
            var Q0;
            Q0 = qSketchRegion(id + "F36", true);
            extrude(context, id + "F37", {"entities" : qUnion([Q0]), "oppositeDirection" : true, "depth" : 6.35 * mm, "offsetDistance" : 25.4 * mm});
        }
        {
            var Q0;
            Q0=makeQuery(id+"F13.opExtrude","SWEPT_FACE",FACE,{"disambiguationData":[OSD([sQuery(id+"F12.wireOp",EDGE,"E24.MirrorCS")])]});
            var sketch = newSketch(context, id + "F38", { "sketchPlane" : qUnion([Q0])});
            skLineSegment(sketch, "E110.bottom", {"start": v(-508, -533.4) * mm, "end": v(-406.4, -533.4) * mm});
            skLineSegment(sketch, "E110.top", {"start": v(-508, -584.2) * mm, "end": v(-406.4, -584.2) * mm});
            skLineSegment(sketch, "E110.left", {"start": v(-508, -533.4) * mm, "end": v(-508, -584.2) * mm});
            skLineSegment(sketch, "E110.right", {"start": v(-406.4, -533.4) * mm, "end": v(-406.4, -584.2) * mm});
            skLineSegment(sketch, "E111", {"start": v(0, 0) * mm, "end": v(0, -1066.8) * mm, "construction": true});
            skLineSegment(sketch, "E112.MirrorCS", {"start": v(406.4, -533.4) * mm, "end": v(406.4, -584.2) * mm});
            skLineSegment(sketch, "E113.MirrorCS", {"start": v(508, -533.4) * mm, "end": v(508, -584.2) * mm});
            skLineSegment(sketch, "E114.MirrorCS", {"start": v(508, -533.4) * mm, "end": v(406.4, -533.4) * mm});
            skLineSegment(sketch, "E115.MirrorCS", {"start": v(508, -584.2) * mm, "end": v(406.4, -584.2) * mm});
            skSolve(sketch);
        }
        {
            var Q0;
            Q0 = qSketchRegion(id + "F38", true);
            var Q1;
            Q1=makeQuery(id+"F17.opExtrude","SWEPT_FACE",FACE,{"disambiguationData":[OSD([sQuery(id+"F16.wireOp",EDGE,"E29.top")])]});
            extrude(context, id + "F39", {"entities" : qUnion([Q0]), "endBound" : BoundingType.UP_TO_SURFACE, "depth" : 25.4 * mm, "endBoundEntityFace" : qUnion([Q1]), "offsetDistance" : 25.4 * mm});
        }
        {
            var Q0;
            Q0=makeQuery(id+"F17.opExtrude","SWEPT_FACE",FACE,{"disambiguationData":[OSD([sQuery(id+"F16.wireOp",EDGE,"E33.MirrorCS")])]});
            var sketch = newSketch(context, id + "F40", { "sketchPlane" : qUnion([Q0])});
            skPoint(sketch, "E116.0", {"position": v(-50.8, -584.2) * mm});
            skPoint(sketch, "E117.0", {"position": v(-50.8, -533.4) * mm});
            skLineSegment(sketch, "E118.bottom", {"start": v(-50.8, -533.4) * mm, "end": v(50.8, -533.4) * mm});
            skLineSegment(sketch, "E118.top", {"start": v(-50.8, -584.2) * mm, "end": v(50.8, -584.2) * mm});
            skLineSegment(sketch, "E118.left", {"start": v(-50.8, -533.4) * mm, "end": v(-50.8, -584.2) * mm});
            skLineSegment(sketch, "E118.right", {"start": v(50.8, -533.4) * mm, "end": v(50.8, -584.2) * mm});
            skSolve(sketch);
        }
        {
            var Q0;
            Q0 = qSketchRegion(id + "F40", true);
            var Q1;
            Q1=makeQuery(id+"F17.opExtrude","SWEPT_FACE",FACE,{"disambiguationData":[OSD([sQuery(id+"F16.wireOp",EDGE,"E29.right")])]});
            extrude(context, id + "F41", {"entities" : qUnion([Q0]), "endBound" : BoundingType.UP_TO_SURFACE, "depth" : 25.4 * mm, "endBoundEntityFace" : qUnion([Q1]), "offsetDistance" : 25.4 * mm});
        }
        {
            var Q0;
            Q0=makeQuery(id+"F15.opExtrude","SWEPT_FACE",FACE,{"disambiguationData":[OSD([sQuery(id+"F14.wireOp",EDGE,"E28.top")])]});
            var sketch = newSketch(context, id + "F42", { "sketchPlane" : qUnion([Q0])});
            skLineSegment(sketch, "E119.bottom", {"start": v(25.4, -533.4) * mm, "end": v(-25.4, -533.4) * mm});
            skLineSegment(sketch, "E119.top", {"start": v(25.4, -584.2) * mm, "end": v(-25.4, -584.2) * mm});
            skLineSegment(sketch, "E119.left", {"start": v(25.4, -533.4) * mm, "end": v(25.4, -584.2) * mm});
            skLineSegment(sketch, "E119.right", {"start": v(-25.4, -533.4) * mm, "end": v(-25.4, -584.2) * mm});
            skSolve(sketch);
        }
        {
            var Q0;
            Q0 = qSketchRegion(id + "F42", true);
            extrude(context, id + "F43", {"entities" : qUnion([Q0]), "depth" : 50.8 * mm, "offsetDistance" : 25.4 * mm});
        }
        {
            var Q0;
            Q0=makeQuery(id+"F13.opExtrude","SWEPT_FACE",FACE,{"disambiguationData":[OSD([sQuery(id+"F12.wireOp",EDGE,"E21.top")])]});
            var sketch = newSketch(context, id + "F44", { "sketchPlane" : qUnion([Q0])});
            skPoint(sketch, "E120.0", {"position": v(-508, -533.4) * mm});
            skPoint(sketch, "E121.0", {"position": v(508, -533.4) * mm});
            skLineSegment(sketch, "E122.bottom", {"start": v(-508, -533.4) * mm, "end": v(-457.2, -533.4) * mm});
            skLineSegment(sketch, "E122.top", {"start": v(-508, -431.8) * mm, "end": v(-457.2, -431.8) * mm});
            skLineSegment(sketch, "E122.left", {"start": v(-508, -533.4) * mm, "end": v(-508, -431.8) * mm});
            skLineSegment(sketch, "E122.right", {"start": v(-457.2, -533.4) * mm, "end": v(-457.2, -431.8) * mm});
            skLineSegment(sketch, "E123.bottom", {"start": v(508, -533.4) * mm, "end": v(457.2, -533.4) * mm});
            skLineSegment(sketch, "E123.top", {"start": v(508, -431.8) * mm, "end": v(457.2, -431.8) * mm});
            skLineSegment(sketch, "E123.left", {"start": v(508, -533.4) * mm, "end": v(508, -431.8) * mm});
            skLineSegment(sketch, "E123.right", {"start": v(457.2, -533.4) * mm, "end": v(457.2, -431.8) * mm});
            skSolve(sketch);
        }
        {
            var Q0;
            Q0 = qSketchRegion(id + "F44", true);
            var Q1;
            Q1=makeQuery(id+"F17.opExtrude","SWEPT_FACE",FACE,{"disambiguationData":[OSD([sQuery(id+"F16.wireOp",EDGE,"E32.MirrorCS")])]});
            extrude(context, id + "F45", {"entities" : qUnion([Q0]), "endBound" : BoundingType.UP_TO_SURFACE, "depth" : 25.4 * mm, "endBoundEntityFace" : qUnion([Q1]), "offsetDistance" : 25.4 * mm});
        }
        {
            var Q0;
            Q0=makeQuery(id+"F17.opExtrude","SWEPT_FACE",FACE,{"disambiguationData":[OSD([sQuery(id+"F16.wireOp",EDGE,"E29.right")])]});
            var sketch = newSketch(context, id + "F46", { "sketchPlane" : qUnion([Q0])});
            skPoint(sketch, "E124.0", {"position": v(-50.8, -533.4) * mm});
            skLineSegment(sketch, "E125.bottom", {"start": v(-50.8, -533.4) * mm, "end": v(0, -533.4) * mm});
            skLineSegment(sketch, "E125.top", {"start": v(-50.8, -431.8) * mm, "end": v(0, -431.8) * mm});
            skLineSegment(sketch, "E125.left", {"start": v(-50.8, -533.4) * mm, "end": v(-50.8, -431.8) * mm});
            skLineSegment(sketch, "E125.right", {"start": v(0, -533.4) * mm, "end": v(0, -431.8) * mm});
            skSolve(sketch);
        }
        {
            var Q0;
            Q0 = qSketchRegion(id + "F46", true);
            var Q1;
            Q1=makeQuery(id+"F17.opExtrude","SWEPT_FACE",FACE,{"disambiguationData":[OSD([sQuery(id+"F16.wireOp",EDGE,"E33.MirrorCS")])]});
            extrude(context, id + "F47", {"entities" : qUnion([Q0]), "endBound" : BoundingType.UP_TO_SURFACE, "depth" : 25.4 * mm, "endBoundEntityFace" : qUnion([Q1]), "offsetDistance" : 25.4 * mm});
        }
        {
            var Q0;
            Q0=makeQuery(id+"F41.opExtrude","SWEPT_FACE",FACE,{"disambiguationData":[OSD([sQuery(id+"F40.wireOp",EDGE,"E118.bottom")])]});
            var sketch = newSketch(context, id + "F48", { "sketchPlane" : qUnion([Q0])});
            skPoint(sketch, "E126.0", {"position": v(-406.4, -50.8) * mm});
            skPoint(sketch, "E127.0", {"position": v(-457.2, -50.8) * mm});
            skPoint(sketch, "E128.0", {"position": v(-457.2, -355.6) * mm});
            skPoint(sketch, "E129.0", {"position": v(-406.4, -355.6) * mm});
            skPoint(sketch, "E130.0", {"position": v(-406.4, -406.4) * mm});
            skPoint(sketch, "E131.0", {"position": v(406.4, -406.4) * mm});
            skPoint(sketch, "E132.0", {"position": v(406.4, -355.6) * mm});
            skPoint(sketch, "E133.0", {"position": v(457.2, -355.6) * mm});
            skPoint(sketch, "E134.0", {"position": v(457.2, -50.8) * mm});
            skPoint(sketch, "E135.0", {"position": v(406.4, -50.8) * mm});
            skLineSegment(sketch, "E136", {"start": v(-406.4, 0) * mm, "end": v(-406.4, -50.8) * mm});
            skLineSegment(sketch, "E137", {"start": v(-457.2, -50.8) * mm, "end": v(-406.4, -50.8) * mm});
            skLineSegment(sketch, "E138", {"start": v(-457.2, -50.8) * mm, "end": v(-457.2, -355.6) * mm});
            skLineSegment(sketch, "E139", {"start": v(-457.2, -355.6) * mm, "end": v(-406.4, -355.6) * mm});
            skLineSegment(sketch, "E140", {"start": v(-406.4, -355.6) * mm, "end": v(-406.4, -406.4) * mm});
            skLineSegment(sketch, "E141", {"start": v(-406.4, -406.4) * mm, "end": v(406.4, -406.4) * mm});
            skLineSegment(sketch, "E142", {"start": v(406.4, -406.4) * mm, "end": v(406.4, -355.6) * mm});
            skLineSegment(sketch, "E143", {"start": v(406.4, -355.6) * mm, "end": v(457.2, -355.6) * mm});
            skLineSegment(sketch, "E144", {"start": v(457.2, -355.6) * mm, "end": v(457.2, -50.8) * mm});
            skLineSegment(sketch, "E145", {"start": v(457.2, -50.8) * mm, "end": v(406.4, -50.8) * mm});
            skLineSegment(sketch, "E146", {"start": v(406.4, -50.8) * mm, "end": v(406.4, 0) * mm});
            skLineSegment(sketch, "E147", {"start": v(-406.4, 0) * mm, "end": v(406.4, 0) * mm});
            skSolve(sketch);
        }
        {
            var Q0;
            Q0 = qSketchRegion(id + "F48", true);
            extrude(context, id + "F49", {"entities" : qUnion([Q0]), "depth" : 6.35 * mm, "offsetDistance" : 25.4 * mm});
        }
        {
            var Q0;
            Q0=makeQuery(id+"F43.opExtrude","SWEPT_FACE",FACE,{"disambiguationData":[OSD([sQuery(id+"F42.wireOp",EDGE,"E119.right")])]});
            var sketch = newSketch(context, id + "F50", { "sketchPlane" : qUnion([Q0])});
            skLineSegment(sketch, "E148", {"start": v(-355.6, -584.2) * mm, "end": v(-355.6, -533.4) * mm});
            skLineSegment(sketch, "E149", {"start": v(-355.6, -533.4) * mm, "end": v(-406.4, -584.2) * mm});
            skLineSegment(sketch, "E150", {"start": v(-406.4, -584.2) * mm, "end": v(-355.6, -584.2) * mm});
            skSolve(sketch);
        }
        {
            var Q0;
            Q0 = qSketchRegion(id + "F50", true);
            extrude(context, id + "F51", {"entities" : qUnion([Q0]), "operationType" : NewBodyOperationType.REMOVE, "oppositeDirection" : true, "depth" : 50.8 * mm, "offsetDistance" : 25.4 * mm});
        }
        {
            var Q0;
            Q0=makeQuery(id+"F5.opExtrude","SWEPT_FACE",FACE,{"disambiguationData":[OSD([sQuery(id+"F4.wireOp",EDGE,"E11.MirrorCS")])]});
            var sketch = newSketch(context, id + "F52", { "sketchPlane" : qUnion([Q0])});
            skLineSegment(sketch, "E151.0", {"start": v(101.6, -1066.8) * mm, "end": v(101.6, 0) * mm});
            skLineSegment(sketch, "E152.bottom", {"start": v(101.6, 0) * mm, "end": v(105.54, 0) * mm});
            skLineSegment(sketch, "E152.top", {"start": v(101.6, -1066.8) * mm, "end": v(109.47, -1066.8) * mm});
            skLineSegment(sketch, "E152.left", {"start": v(101.6, 0) * mm, "end": v(101.6, -1066.8) * mm});
            skLineSegment(sketch, "E152.right", {"start": v(109.47, -7.87) * mm, "end": v(109.47, -133.41) * mm});
            skLineSegment(sketch, "E153", {"start": v(105.54, 0) * mm, "end": v(105.54, -1066.8) * mm, "construction": true});
            skLineSegment(sketch, "E154", {"start": v(101.6, -141.29) * mm, "end": v(105.54, -141.29) * mm, "construction": true});
            skLineSegment(sketch, "E155", {"start": v(105.54, 0) * mm, "end": v(109.47, -7.87) * mm});
            skPoint(sketch, "E156.orphan", {"position": v(109.47, 0) * mm});
            skLineSegment(sketch, "E157", {"start": v(105.54, -141.29) * mm, "end": v(109.47, -133.41) * mm});
            skLineSegment(sketch, "E158", {"start": v(105.54, -141.29) * mm, "end": v(109.47, -149.16) * mm});
            skLineSegment(sketch, "E159.trimOffspring", {"start": v(109.47, -149.16) * mm, "end": v(109.47, -274.7) * mm});
            skPoint(sketch, "E160.orphan", {"position": v(109.47, -141.29) * mm});
            skLineSegment(sketch, "E161.0.1.0", {"start": v(105.54, -282.58) * mm, "end": v(109.47, -274.7) * mm});
            skLineSegment(sketch, "E161.0.1.1", {"start": v(105.54, -282.58) * mm, "end": v(109.47, -290.45) * mm});
            skLineSegment(sketch, "E161.0.2.0", {"start": v(105.54, -423.86) * mm, "end": v(109.47, -415.99) * mm});
            skLineSegment(sketch, "E161.0.2.1", {"start": v(105.54, -423.86) * mm, "end": v(109.47, -431.74) * mm});
            skLineSegment(sketch, "E161.0.3.0", {"start": v(105.54, -565.15) * mm, "end": v(109.47, -557.28) * mm});
            skLineSegment(sketch, "E161.0.3.1", {"start": v(105.54, -565.15) * mm, "end": v(109.47, -573.02) * mm});
            skLineSegment(sketch, "E161.0.4.0", {"start": v(105.54, -706.44) * mm, "end": v(109.47, -698.56) * mm});
            skLineSegment(sketch, "E161.0.4.1", {"start": v(105.54, -706.44) * mm, "end": v(109.47, -714.31) * mm});
            skLineSegment(sketch, "E161.0.5.0", {"start": v(105.54, -847.73) * mm, "end": v(109.47, -839.85) * mm});
            skLineSegment(sketch, "E161.0.5.1", {"start": v(105.54, -847.73) * mm, "end": v(109.47, -855.6) * mm});
            skLineSegment(sketch, "E161.0.6.0", {"start": v(105.54, -989.01) * mm, "end": v(109.47, -981.14) * mm});
            skLineSegment(sketch, "E161.0.6.1", {"start": v(105.54, -989.01) * mm, "end": v(109.47, -996.89) * mm});
            skLineSegment(sketch, "E161.direction1", {"start": v(105.54, -149.16) * mm, "end": v(109.47, -149.16) * mm, "construction": true});
            skLineSegment(sketch, "E161.direction2", {"start": v(109.47, -149.16) * mm, "end": v(109.47, -274.7) * mm, "construction": true});
            skLineSegment(sketch, "E162.trimOffspring", {"start": v(109.47, -290.45) * mm, "end": v(109.47, -415.99) * mm});
            skLineSegment(sketch, "E163.trimOffspring", {"start": v(109.47, -431.74) * mm, "end": v(109.47, -557.28) * mm});
            skLineSegment(sketch, "E164.trimOffspring", {"start": v(109.47, -573.02) * mm, "end": v(109.47, -698.56) * mm});
            skLineSegment(sketch, "E165.trimOffspring", {"start": v(109.47, -714.31) * mm, "end": v(109.47, -839.85) * mm});
            skLineSegment(sketch, "E166.trimOffspring", {"start": v(109.47, -855.6) * mm, "end": v(109.47, -981.14) * mm});
            skLineSegment(sketch, "E167.trimOffspring", {"start": v(109.47, -996.89) * mm, "end": v(109.47, -1122.43) * mm});
            skLineSegment(sketch, "E168.trimOffspring", {"start": v(109.47, -1138.17) * mm, "end": v(109.47, -1263.71) * mm});
            skLineSegment(sketch, "E169.trimOffspring", {"start": v(109.47, -1279.46) * mm, "end": v(109.47, -1405) * mm});
            skLineSegment(sketch, "E170.trimOffspring", {"start": v(109.47, -1420.75) * mm, "end": v(109.47, -1546.29) * mm});
            skLineSegment(sketch, "E171.trimOffspring", {"start": v(109.47, -1066.8) * mm, "end": v(109.47, -1562.04) * mm});
            skSolve(sketch);
        }
        {
            var Q0;
            Q0 = qSketchRegion(id + "F52", true);
            var Q1;
            Q1=makeQuery(id+"F5.opExtrude","SWEPT_FACE",FACE,{"disambiguationData":[OSD([sQuery(id+"F4.wireOp",EDGE,"E6.left")])]});
            extrude(context, id + "F53", {"entities" : qUnion([Q0]), "endBound" : BoundingType.UP_TO_SURFACE, "oppositeDirection" : true, "depth" : 25.4 * mm, "endBoundEntityFace" : qUnion([Q1]), "offsetDistance" : 25.4 * mm});
        }
        {
            var Q0;
            Q0=makeQuery(id+"F53.opExtrude","SWEPT_FACE",FACE,{"disambiguationData":[OSD([sQuery(id+"F52.wireOp",EDGE,"E152.top")])]});
            var sketch = newSketch(context, id + "F54", { "sketchPlane" : qUnion([Q0])});
            skLineSegment(sketch, "E172", {"start": v(0, 0) * mm, "end": v(0, -304.8) * mm, "construction": true});
            skPoint(sketch, "E173.0", {"position": v(863.6, -101.6) * mm});
            skLineSegment(sketch, "E174", {"start": v(863.6, -101.6) * mm, "end": v(871.47, -109.47) * mm});
            skLineSegment(sketch, "E175", {"start": v(871.47, -109.47) * mm, "end": v(914.4, -109.47) * mm});
            skLineSegment(sketch, "E176", {"start": v(914.4, -109.47) * mm, "end": v(914.4, -101.6) * mm});
            skLineSegment(sketch, "E177", {"start": v(914.4, -101.6) * mm, "end": v(863.6, -101.6) * mm});
            skLineSegment(sketch, "E178.MirrorCS", {"start": v(-914.4, -109.47) * mm, "end": v(-914.4, -101.6) * mm});
            skLineSegment(sketch, "E179.MirrorCS", {"start": v(-863.6, -101.6) * mm, "end": v(-871.47, -109.47) * mm});
            skPoint(sketch, "E180.MirrorP", {"position": v(-863.6, -101.6) * mm});
            skLineSegment(sketch, "E181.MirrorCS", {"start": v(-871.47, -109.47) * mm, "end": v(-914.4, -109.47) * mm});
            skLineSegment(sketch, "E182.MirrorCS", {"start": v(-914.4, -101.6) * mm, "end": v(-863.6, -101.6) * mm});
            skSolve(sketch);
        }
        {
            var Q0;
            Q0 = qSketchRegion(id + "F54", true);
            var Q1;
            Q1=qCreatedBy(makeId("Top.planeOp"),FACE);
            extrude(context, id + "F55", {"entities" : qUnion([Q0]), "operationType" : NewBodyOperationType.REMOVE, "endBound" : BoundingType.UP_TO_SURFACE, "oppositeDirection" : true, "depth" : 25.4 * mm, "endBoundEntityFace" : qUnion([Q1]), "offsetDistance" : 25.4 * mm});
        }
        {
            var Q0;
            Q0=makeQuery(id+"F5.opExtrude","SWEPT_FACE",FACE,{"disambiguationData":[OSD([sQuery(id+"F4.wireOp",EDGE,"E6.top")])]});
            var sketch = newSketch(context, id + "F56", { "sketchPlane" : qUnion([Q0])});
            skLineSegment(sketch, "E183.0", {"start": v(863.6, -1066.8) * mm, "end": v(863.6, 0) * mm});
            skLineSegment(sketch, "E184", {"start": v(863.6, 0) * mm, "end": v(863.6, -1066.8) * mm});
            skLineSegment(sketch, "E185", {"start": v(863.6, -1066.8) * mm, "end": v(871.47, -1066.8) * mm});
            skLineSegment(sketch, "E186", {"start": v(871.47, -1562.04) * mm, "end": v(871.47, -1066.8) * mm});
            skLineSegment(sketch, "E187", {"start": v(867.54, 0) * mm, "end": v(863.6, 0) * mm});
            skLineSegment(sketch, "E188", {"start": v(867.54, 0) * mm, "end": v(871.47, -7.87) * mm});
            skLineSegment(sketch, "E189", {"start": v(867.54, 0) * mm, "end": v(867.54, -1066.8) * mm, "construction": true});
            skPoint(sketch, "E190.orphan", {"position": v(871.47, 0) * mm});
            skLineSegment(sketch, "E191", {"start": v(863.6, -141.29) * mm, "end": v(867.54, -141.29) * mm, "construction": true});
            skLineSegment(sketch, "E192", {"start": v(867.54, -141.29) * mm, "end": v(871.47, -133.41) * mm});
            skLineSegment(sketch, "E193", {"start": v(867.54, -141.29) * mm, "end": v(871.47, -149.16) * mm});
            skLineSegment(sketch, "E194.trimOffspring", {"start": v(871.47, -133.41) * mm, "end": v(871.47, -7.87) * mm});
            skPoint(sketch, "E195.orphan", {"position": v(871.47, -141.29) * mm});
            skLineSegment(sketch, "E196.0.1.0", {"start": v(867.54, -282.58) * mm, "end": v(871.47, -274.7) * mm});
            skLineSegment(sketch, "E196.0.1.1", {"start": v(867.54, -282.58) * mm, "end": v(871.47, -290.45) * mm});
            skLineSegment(sketch, "E196.0.2.0", {"start": v(867.54, -423.86) * mm, "end": v(871.47, -415.99) * mm});
            skLineSegment(sketch, "E196.0.2.1", {"start": v(867.54, -423.86) * mm, "end": v(871.47, -431.74) * mm});
            skLineSegment(sketch, "E196.0.3.0", {"start": v(867.54, -565.15) * mm, "end": v(871.47, -557.28) * mm});
            skLineSegment(sketch, "E196.0.3.1", {"start": v(867.54, -565.15) * mm, "end": v(871.47, -573.02) * mm});
            skLineSegment(sketch, "E196.0.4.0", {"start": v(867.54, -706.44) * mm, "end": v(871.47, -698.56) * mm});
            skLineSegment(sketch, "E196.0.4.1", {"start": v(867.54, -706.44) * mm, "end": v(871.47, -714.31) * mm});
            skLineSegment(sketch, "E196.0.5.0", {"start": v(867.54, -847.73) * mm, "end": v(871.47, -839.85) * mm});
            skLineSegment(sketch, "E196.0.5.1", {"start": v(867.54, -847.73) * mm, "end": v(871.47, -855.6) * mm});
            skLineSegment(sketch, "E196.0.6.0", {"start": v(867.54, -989.01) * mm, "end": v(871.47, -981.14) * mm});
            skLineSegment(sketch, "E196.0.6.1", {"start": v(867.54, -989.01) * mm, "end": v(871.47, -996.89) * mm});
            skLineSegment(sketch, "E196.direction1", {"start": v(867.54, -141.29) * mm, "end": v(867.54, -141.29) * mm});
            skLineSegment(sketch, "E196.direction2", {"start": v(867.54, -141.29) * mm, "end": v(867.54, -282.58) * mm, "construction": true});
            skLineSegment(sketch, "E197.trimOffspring", {"start": v(871.47, -274.7) * mm, "end": v(871.47, -149.16) * mm});
            skLineSegment(sketch, "E198.trimOffspring", {"start": v(871.47, -415.99) * mm, "end": v(871.47, -290.45) * mm});
            skLineSegment(sketch, "E199.trimOffspring", {"start": v(871.47, -557.28) * mm, "end": v(871.47, -431.74) * mm});
            skLineSegment(sketch, "E200.trimOffspring", {"start": v(871.47, -698.56) * mm, "end": v(871.47, -573.02) * mm});
            skLineSegment(sketch, "E201.trimOffspring", {"start": v(871.47, -839.85) * mm, "end": v(871.47, -714.31) * mm});
            skLineSegment(sketch, "E202.trimOffspring", {"start": v(871.47, -981.14) * mm, "end": v(871.47, -855.6) * mm});
            skLineSegment(sketch, "E203.trimOffspring", {"start": v(871.47, -1122.43) * mm, "end": v(871.47, -996.89) * mm});
            skLineSegment(sketch, "E204.trimOffspring", {"start": v(871.47, -1263.71) * mm, "end": v(871.47, -1138.17) * mm});
            skLineSegment(sketch, "E205.trimOffspring", {"start": v(871.47, -1405) * mm, "end": v(871.47, -1279.46) * mm});
            skLineSegment(sketch, "E206.trimOffspring", {"start": v(871.47, -1546.29) * mm, "end": v(871.47, -1420.75) * mm});
            skSolve(sketch);
        }
        {
            var Q0;
            Q0 = qSketchRegion(id + "F56", true);
            var Q1;
            Q1=makeQuery(id+"F55.boolean.opBoolean","COPY",FACE,{"derivedFrom":makeQuery(id+"F55.opExtrude","SWEPT_FACE",FACE,{"disambiguationData":[OSD([sQuery(id+"F54.wireOp",EDGE,"d1cb4c1c-491e-46d1-ae2b-8dbab645d63a0.MirrorCS")])]})});
            extrude(context, id + "F57", {"entities" : qUnion([Q0]), "endBound" : BoundingType.UP_TO_NEXT, "depth" : 25.4 * mm, "endBoundEntityFace" : qUnion([Q1]), "offsetDistance" : 25.4 * mm});
        }
        {
            var Q0;
            Q0=makeQuery(id+"F5.opExtrude","SWEPT_FACE",FACE,{"disambiguationData":[OSD([sQuery(id+"F4.wireOp",EDGE,"E9.MirrorCS")])]});
            var sketch = newSketch(context, id + "F58", { "sketchPlane" : qUnion([Q0])});
            skLineSegment(sketch, "E207.0", {"start": v(-863.6, -1066.8) * mm, "end": v(-863.6, 0) * mm});
            skLineSegment(sketch, "E208", {"start": v(-863.6, 0) * mm, "end": v(-863.6, -1066.8) * mm});
            skLineSegment(sketch, "E209", {"start": v(-863.6, -1066.8) * mm, "end": v(-871.47, -1066.8) * mm});
            skLineSegment(sketch, "E210", {"start": v(-871.47, -1562.04) * mm, "end": v(-871.47, -1066.8) * mm});
            skLineSegment(sketch, "E211", {"start": v(-867.54, 0) * mm, "end": v(-863.6, 0) * mm});
            skLineSegment(sketch, "E212", {"start": v(-867.54, 0) * mm, "end": v(-867.54, -1066.8) * mm, "construction": true});
            skLineSegment(sketch, "E213", {"start": v(-863.6, -141.29) * mm, "end": v(-867.54, -141.29) * mm, "construction": true});
            skLineSegment(sketch, "E214", {"start": v(-867.54, 0) * mm, "end": v(-871.47, -7.87) * mm});
            skPoint(sketch, "E215.orphan", {"position": v(-871.47, 0) * mm});
            skLineSegment(sketch, "E216", {"start": v(-871.47, -133.41) * mm, "end": v(-867.54, -141.29) * mm});
            skLineSegment(sketch, "E217", {"start": v(-867.54, -141.29) * mm, "end": v(-871.47, -149.16) * mm});
            skLineSegment(sketch, "E218.trimOffspring", {"start": v(-871.47, -133.41) * mm, "end": v(-871.47, -7.87) * mm});
            skPoint(sketch, "E219.orphan", {"position": v(-871.47, -141.29) * mm});
            skLineSegment(sketch, "E220.0.1.0", {"start": v(-871.47, -274.7) * mm, "end": v(-867.54, -282.58) * mm});
            skLineSegment(sketch, "E220.0.1.1", {"start": v(-867.54, -282.58) * mm, "end": v(-871.47, -290.45) * mm});
            skLineSegment(sketch, "E220.0.2.0", {"start": v(-871.47, -415.99) * mm, "end": v(-867.54, -423.86) * mm});
            skLineSegment(sketch, "E220.0.2.1", {"start": v(-867.54, -423.86) * mm, "end": v(-871.47, -431.74) * mm});
            skLineSegment(sketch, "E220.0.3.0", {"start": v(-871.47, -557.28) * mm, "end": v(-867.54, -565.15) * mm});
            skLineSegment(sketch, "E220.0.3.1", {"start": v(-867.54, -565.15) * mm, "end": v(-871.47, -573.02) * mm});
            skLineSegment(sketch, "E220.0.4.0", {"start": v(-871.47, -698.56) * mm, "end": v(-867.54, -706.44) * mm});
            skLineSegment(sketch, "E220.0.4.1", {"start": v(-867.54, -706.44) * mm, "end": v(-871.47, -714.31) * mm});
            skLineSegment(sketch, "E220.direction1", {"start": v(-867.54, -149.16) * mm, "end": v(-871.47, -149.16) * mm, "construction": true});
            skLineSegment(sketch, "E220.direction2", {"start": v(-871.47, -149.16) * mm, "end": v(-871.47, -274.7) * mm, "construction": true});
            skLineSegment(sketch, "E221.trimOffspring", {"start": v(-871.47, -415.99) * mm, "end": v(-871.47, -290.45) * mm});
            skLineSegment(sketch, "E222.trimOffspring", {"start": v(-871.47, -274.7) * mm, "end": v(-871.47, -149.16) * mm});
            skLineSegment(sketch, "E223.trimOffspring", {"start": v(-871.47, -557.28) * mm, "end": v(-871.47, -431.74) * mm});
            skLineSegment(sketch, "E224.trimOffspring", {"start": v(-871.47, -698.56) * mm, "end": v(-871.47, -573.02) * mm});
            skLineSegment(sketch, "E225.trimOffspring", {"start": v(-871.47, -839.85) * mm, "end": v(-871.47, -714.31) * mm});
            skLineSegment(sketch, "E226.trimOffspring", {"start": v(-871.47, -981.14) * mm, "end": v(-871.47, -855.6) * mm});
            skLineSegment(sketch, "E227.trimOffspring", {"start": v(-871.47, -1263.71) * mm, "end": v(-871.47, -1138.17) * mm});
            skLineSegment(sketch, "E228.trimOffspring", {"start": v(-871.47, -1405) * mm, "end": v(-871.47, -1279.46) * mm});
            skLineSegment(sketch, "E229.trimOffspring", {"start": v(-871.47, -1546.29) * mm, "end": v(-871.47, -1420.75) * mm});
            skLineSegment(sketch, "E230.trimOffspring", {"start": v(-871.47, -1122.43) * mm, "end": v(-871.47, -996.89) * mm});
            skLineSegment(sketch, "E231.0.0.5", {"start": v(-871.47, -839.85) * mm, "end": v(-867.54, -847.73) * mm});
            skLineSegment(sketch, "E231.3.0.5", {"start": v(-867.54, -847.73) * mm, "end": v(-871.47, -855.6) * mm});
            skLineSegment(sketch, "E231.0.0.6", {"start": v(-871.47, -981.14) * mm, "end": v(-867.54, -989.01) * mm});
            skLineSegment(sketch, "E231.3.0.6", {"start": v(-867.54, -989.01) * mm, "end": v(-871.47, -996.89) * mm});
            skSolve(sketch);
        }
        {
            var Q0;
            Q0 = qSketchRegion(id + "F58", true);
            var Q1;
            Q1=makeQuery(id+"F55.boolean.opBoolean","COPY",FACE,{"derivedFrom":makeQuery(id+"F55.opExtrude","SWEPT_FACE",FACE,{"disambiguationData":[OSD([sQuery(id+"F54.wireOp",EDGE,"2yZ4iRki-qh2Y-Grbb-o7WT-W1c75ycgdIp5")])]})});
            extrude(context, id + "F59", {"entities" : qUnion([Q0]), "endBound" : BoundingType.UP_TO_NEXT, "depth" : 25.4 * mm, "endBoundEntityFace" : qUnion([Q1]), "offsetDistance" : 25.4 * mm});
        }
        {
            var Q0;
            Q0=makeQuery(id+"F59.opExtrude","SWEPT_FACE",FACE,{"disambiguationData":[OSD([sQuery(id+"F58.wireOp",EDGE,"E218.trimOffspring")])]});
            var sketch = newSketch(context, id + "F60", { "sketchPlane" : qUnion([Q0])});
            skPoint(sketch, "E232.0", {"position": v(-355.6, 0) * mm});
            skPoint(sketch, "E233.0", {"position": v(109.47, -1066.8) * mm});
            skLineSegment(sketch, "E234.bottom", {"start": v(-355.6, 0) * mm, "end": v(134.87, 0) * mm});
            skLineSegment(sketch, "E234.top", {"start": v(-355.6, -50.8) * mm, "end": v(134.87, -50.8) * mm});
            skLineSegment(sketch, "E234.left", {"start": v(-355.6, 0) * mm, "end": v(-355.6, -50.8) * mm});
            skLineSegment(sketch, "E234.right", {"start": v(134.87, 0) * mm, "end": v(134.87, -50.8) * mm});
            skLineSegment(sketch, "E235.bottom", {"start": v(-355.6, -1066.8) * mm, "end": v(134.87, -1066.8) * mm});
            skLineSegment(sketch, "E235.top", {"start": v(-355.6, -1016) * mm, "end": v(134.87, -1016) * mm});
            skLineSegment(sketch, "E235.left", {"start": v(-355.6, -1066.8) * mm, "end": v(-355.6, -1016) * mm});
            skLineSegment(sketch, "E235.right", {"start": v(134.87, -1066.8) * mm, "end": v(134.87, -1016) * mm});
            skSolve(sketch);
        }
        {
            var Q0;
            Q0 = qSketchRegion(id + "F60", true);
            extrude(context, id + "F61", {"entities" : qUnion([Q0]), "depth" : 25.4 * mm, "offsetDistance" : 25.4 * mm});
        }
        {
            var Q0;
            Q0=makeQuery(id+"F59.opExtrude","SWEPT_FACE",FACE,{"disambiguationData":[OSD([sQuery(id+"F58.wireOp",EDGE,"E218.trimOffspring")])]});
            var sketch = newSketch(context, id + "F62", { "sketchPlane" : qUnion([Q0])});
            skPoint(sketch, "E236.0", {"position": v(134.87, -1016) * mm});
            skPoint(sketch, "E237.0", {"position": v(134.87, -50.8) * mm});
            skPoint(sketch, "E238.0", {"position": v(-355.6, -50.8) * mm});
            skPoint(sketch, "E239.0", {"position": v(-355.6, -1016) * mm});
            skLineSegment(sketch, "E240.bottom", {"start": v(-355.6, -50.8) * mm, "end": v(-304.8, -50.8) * mm});
            skLineSegment(sketch, "E240.top", {"start": v(-355.6, -1016) * mm, "end": v(-304.8, -1016) * mm});
            skLineSegment(sketch, "E240.left", {"start": v(-355.6, -50.8) * mm, "end": v(-355.6, -1016) * mm});
            skLineSegment(sketch, "E240.right", {"start": v(-304.8, -50.8) * mm, "end": v(-304.8, -1016) * mm});
            skLineSegment(sketch, "E241.bottom", {"start": v(134.87, -50.8) * mm, "end": v(84.07, -50.8) * mm});
            skLineSegment(sketch, "E241.top", {"start": v(134.87, -1016) * mm, "end": v(84.07, -1016) * mm});
            skLineSegment(sketch, "E241.left", {"start": v(134.87, -50.8) * mm, "end": v(134.87, -1016) * mm});
            skLineSegment(sketch, "E241.right", {"start": v(84.07, -50.8) * mm, "end": v(84.07, -1016) * mm});
            skSolve(sketch);
        }
        {
            var Q0;
            Q0 = qSketchRegion(id + "F62", true);
            extrude(context, id + "F63", {"entities" : qUnion([Q0]), "depth" : 25.4 * mm, "offsetDistance" : 25.4 * mm});
        }
        {
            var Q0;
            Q0=makeQuery(id+"F57.opExtrude","SWEPT_FACE",FACE,{"disambiguationData":[OSD([sQuery(id+"F56.wireOp",EDGE,"E194.trimOffspring")])]});
            var sketch = newSketch(context, id + "F64", { "sketchPlane" : qUnion([Q0])});
            skPoint(sketch, "E242.0", {"position": v(355.6, 0) * mm});
            skPoint(sketch, "E243.0", {"position": v(355.6, -1066.8) * mm});
            skLineSegment(sketch, "E244.bottom", {"start": v(355.6, -1066.8) * mm, "end": v(-134.87, -1066.8) * mm});
            skLineSegment(sketch, "E244.top", {"start": v(355.6, -1016) * mm, "end": v(-134.87, -1016) * mm});
            skLineSegment(sketch, "E244.left", {"start": v(355.6, -1066.8) * mm, "end": v(355.6, -1016) * mm});
            skLineSegment(sketch, "E244.right", {"start": v(-134.87, -1066.8) * mm, "end": v(-134.87, -1016) * mm});
            skLineSegment(sketch, "E245.bottom", {"start": v(355.6, 0) * mm, "end": v(-134.87, 0) * mm});
            skLineSegment(sketch, "E245.top", {"start": v(355.6, -50.8) * mm, "end": v(-134.87, -50.8) * mm});
            skLineSegment(sketch, "E245.left", {"start": v(355.6, 0) * mm, "end": v(355.6, -50.8) * mm});
            skLineSegment(sketch, "E245.right", {"start": v(-134.87, 0) * mm, "end": v(-134.87, -50.8) * mm});
            skSolve(sketch);
        }
        {
            var Q0;
            Q0 = qSketchRegion(id + "F64", true);
            extrude(context, id + "F65", {"entities" : qUnion([Q0]), "depth" : 25.4 * mm, "offsetDistance" : 25.4 * mm});
        }
        {
            var Q0;
            Q0=makeQuery(id+"F57.opExtrude","SWEPT_FACE",FACE,{"disambiguationData":[OSD([sQuery(id+"F56.wireOp",EDGE,"E194.trimOffspring")])]});
            var sketch = newSketch(context, id + "F66", { "sketchPlane" : qUnion([Q0])});
            skPoint(sketch, "E246.0", {"position": v(-134.87, -50.8) * mm});
            skPoint(sketch, "E247.0", {"position": v(355.6, -50.8) * mm});
            skPoint(sketch, "E248.0", {"position": v(-134.87, -1016) * mm});
            skPoint(sketch, "E249.0", {"position": v(355.6, -1016) * mm});
            skLineSegment(sketch, "E250.bottom", {"start": v(-134.87, -50.8) * mm, "end": v(-84.07, -50.8) * mm});
            skLineSegment(sketch, "E250.top", {"start": v(-134.87, -1016) * mm, "end": v(-84.07, -1016) * mm});
            skLineSegment(sketch, "E250.left", {"start": v(-134.87, -50.8) * mm, "end": v(-134.87, -1016) * mm});
            skLineSegment(sketch, "E250.right", {"start": v(-84.07, -50.8) * mm, "end": v(-84.07, -1016) * mm});
            skLineSegment(sketch, "E251.bottom", {"start": v(355.6, -1016) * mm, "end": v(304.8, -1016) * mm});
            skLineSegment(sketch, "E251.top", {"start": v(355.6, -50.8) * mm, "end": v(304.8, -50.8) * mm});
            skLineSegment(sketch, "E251.left", {"start": v(355.6, -1016) * mm, "end": v(355.6, -50.8) * mm});
            skLineSegment(sketch, "E251.right", {"start": v(304.8, -1016) * mm, "end": v(304.8, -50.8) * mm});
            skSolve(sketch);
        }
        {
            var Q0;
            Q0 = qSketchRegion(id + "F66", true);
            extrude(context, id + "F67", {"entities" : qUnion([Q0]), "depth" : 25.4 * mm, "offsetDistance" : 25.4 * mm});
        }
        {
            var Q0;
            Q0=makeQuery(id+"F53.opExtrude","SWEPT_FACE",FACE,{"disambiguationData":[OSD([sQuery(id+"F52.wireOp",EDGE,"E152.right")])]});
            var sketch = newSketch(context, id + "F68", { "sketchPlane" : qUnion([Q0])});
            skPoint(sketch, "E252.0", {"position": v(871.47, 0) * mm});
            skPoint(sketch, "E253.0", {"position": v(871.47, -50.8) * mm});
            skPoint(sketch, "E254.0", {"position": v(-871.47, 0) * mm});
            skPoint(sketch, "E255.0", {"position": v(-871.47, -50.8) * mm});
            skPoint(sketch, "E256.0", {"position": v(-871.47, -1016) * mm});
            skPoint(sketch, "E257.0", {"position": v(-871.47, -1066.8) * mm});
            skPoint(sketch, "E258.0", {"position": v(871.47, -1016) * mm});
            skPoint(sketch, "E259.0", {"position": v(871.47, -1066.8) * mm});
            skLineSegment(sketch, "E260.bottom", {"start": v(-871.47, 0) * mm, "end": v(871.47, 0) * mm});
            skLineSegment(sketch, "E260.top", {"start": v(-871.47, -50.8) * mm, "end": v(871.47, -50.8) * mm});
            skLineSegment(sketch, "E260.left", {"start": v(-871.47, 0) * mm, "end": v(-871.47, -50.8) * mm});
            skLineSegment(sketch, "E260.right", {"start": v(871.47, 0) * mm, "end": v(871.47, -50.8) * mm});
            skLineSegment(sketch, "E261.bottom", {"start": v(871.47, -1016) * mm, "end": v(-871.47, -1016) * mm});
            skLineSegment(sketch, "E261.top", {"start": v(871.47, -1066.8) * mm, "end": v(-871.47, -1066.8) * mm});
            skLineSegment(sketch, "E261.left", {"start": v(871.47, -1016) * mm, "end": v(871.47, -1066.8) * mm});
            skLineSegment(sketch, "E261.right", {"start": v(-871.47, -1016) * mm, "end": v(-871.47, -1066.8) * mm});
            skSolve(sketch);
        }
        {
            var Q0;
            Q0 = qSketchRegion(id + "F68", true);
            extrude(context, id + "F69", {"entities" : qUnion([Q0]), "depth" : 25.4 * mm, "offsetDistance" : 25.4 * mm});
        }
        {
            var Q0;
            Q0=makeQuery(id+"F53.opExtrude","SWEPT_FACE",FACE,{"disambiguationData":[OSD([sQuery(id+"F52.wireOp",EDGE,"E152.right")])]});
            var sketch = newSketch(context, id + "F70", { "sketchPlane" : qUnion([Q0])});
            skPoint(sketch, "E262.0", {"position": v(-871.47, -50.8) * mm});
            skPoint(sketch, "E263.0", {"position": v(-871.47, -1016) * mm});
            skPoint(sketch, "E264.0", {"position": v(871.47, -1016) * mm});
            skPoint(sketch, "E265.0", {"position": v(871.47, -50.8) * mm});
            skLineSegment(sketch, "E266.bottom", {"start": v(-871.47, -50.8) * mm, "end": v(-820.67, -50.8) * mm});
            skLineSegment(sketch, "E266.top", {"start": v(-871.47, -1016) * mm, "end": v(-820.67, -1016) * mm});
            skLineSegment(sketch, "E266.left", {"start": v(-871.47, -50.8) * mm, "end": v(-871.47, -1016) * mm});
            skLineSegment(sketch, "E266.right", {"start": v(-820.67, -50.8) * mm, "end": v(-820.67, -1016) * mm});
            skLineSegment(sketch, "E267.bottom", {"start": v(871.47, -50.8) * mm, "end": v(820.67, -50.8) * mm});
            skLineSegment(sketch, "E267.top", {"start": v(871.47, -1016) * mm, "end": v(820.67, -1016) * mm});
            skLineSegment(sketch, "E267.left", {"start": v(871.47, -50.8) * mm, "end": v(871.47, -1016) * mm});
            skLineSegment(sketch, "E267.right", {"start": v(820.67, -50.8) * mm, "end": v(820.67, -1016) * mm});
            skSolve(sketch);
        }
        {
            var Q0;
            Q0 = qSketchRegion(id + "F70", true);
            extrude(context, id + "F71", {"entities" : qUnion([Q0]), "depth" : 25.4 * mm, "offsetDistance" : 25.4 * mm});
        }
        {
            var Q0;
            Q0=makeQuery(id+"F59.opExtrude","SWEPT_FACE",FACE,{"disambiguationData":[OSD([sQuery(id+"F58.wireOp",EDGE,"E218.trimOffspring")])]});
            var sketch = newSketch(context, id + "F72", { "sketchPlane" : qUnion([Q0])});
            skPoint(sketch, "E268.0", {"position": v(-304.8, -1016) * mm});
            skPoint(sketch, "E269.0", {"position": v(84.07, -50.8) * mm});
            skLineSegment(sketch, "E270", {"start": v(-304.8, -1016) * mm, "end": v(84.07, -50.8) * mm, "construction": true});
            skLineSegment(sketch, "E271", {"start": v(-304.8, -1016) * mm, "end": v(-304.8, -948.03) * mm});
            skLineSegment(sketch, "E272", {"start": v(-304.8, -948.03) * mm, "end": v(56.69, -50.8) * mm});
            skLineSegment(sketch, "E273", {"start": v(56.69, -50.8) * mm, "end": v(84.07, -50.8) * mm});
            skLineSegment(sketch, "E274", {"start": v(84.07, -118.77) * mm, "end": v(84.07, -50.8) * mm});
            skLineSegment(sketch, "E275", {"start": v(84.07, -50.8) * mm, "end": v(56.69, -50.8) * mm});
            skLineSegment(sketch, "E276", {"start": v(84.07, -118.77) * mm, "end": v(-277.42, -1016) * mm});
            skLineSegment(sketch, "E277", {"start": v(-304.8, -948.03) * mm, "end": v(-304.8, -1016) * mm});
            skLineSegment(sketch, "E278", {"start": v(-304.8, -1016) * mm, "end": v(-277.42, -1016) * mm});
            skSolve(sketch);
        }
        {
            var Q0;
            Q0 = qSketchRegion(id + "F72", true);
            extrude(context, id + "F73", {"entities" : qUnion([Q0]), "depth" : 25.4 * mm, "offsetDistance" : 25.4 * mm});
        }
        {
            var Q0;
            Q0=makeQuery(id+"F57.opExtrude","SWEPT_FACE",FACE,{"disambiguationData":[OSD([sQuery(id+"F56.wireOp",EDGE,"E194.trimOffspring")])]});
            var sketch = newSketch(context, id + "F74", { "sketchPlane" : qUnion([Q0])});
            skPoint(sketch, "E279.0", {"position": v(-84.07, -50.8) * mm});
            skPoint(sketch, "E280.0", {"position": v(304.8, -1016) * mm});
            skLineSegment(sketch, "E281", {"start": v(-84.07, -50.8) * mm, "end": v(304.8, -1016) * mm, "construction": true});
            skLineSegment(sketch, "E282", {"start": v(-84.07, -50.8) * mm, "end": v(-56.69, -50.8) * mm});
            skLineSegment(sketch, "E283", {"start": v(-56.69, -50.8) * mm, "end": v(304.8, -948.03) * mm});
            skLineSegment(sketch, "E284", {"start": v(304.8, -1016) * mm, "end": v(304.8, -948.03) * mm});
            skLineSegment(sketch, "E285", {"start": v(304.8, -1016) * mm, "end": v(277.42, -1016) * mm});
            skLineSegment(sketch, "E286", {"start": v(277.42, -1016) * mm, "end": v(-84.07, -118.77) * mm});
            skLineSegment(sketch, "E287", {"start": v(-84.07, -118.77) * mm, "end": v(-84.07, -50.8) * mm});
            skSolve(sketch);
        }
        {
            var Q0;
            Q0 = qSketchRegion(id + "F74", true);
            extrude(context, id + "F75", {"entities" : qUnion([Q0]), "depth" : 25.4 * mm, "offsetDistance" : 25.4 * mm});
        }
        {
            var Q0;
            Q0=makeQuery(id+"F53.opExtrude","SWEPT_FACE",FACE,{"disambiguationData":[OSD([sQuery(id+"F52.wireOp",EDGE,"E152.right")])]});
            var sketch = newSketch(context, id + "F76", { "sketchPlane" : qUnion([Q0])});
            skPoint(sketch, "E288.0", {"position": v(820.67, -50.8) * mm});
            skPoint(sketch, "E289.0", {"position": v(-820.67, -1016) * mm});
            skLineSegment(sketch, "E290", {"start": v(-820.67, -1016) * mm, "end": v(820.67, -50.8) * mm, "construction": true});
            skLineSegment(sketch, "E291", {"start": v(820.67, -50.8) * mm, "end": v(820.67, -1016) * mm, "construction": true});
            skLineSegment(sketch, "E292", {"start": v(-820.67, -1016) * mm, "end": v(820.67, -1016) * mm, "construction": true});
            skLineSegment(sketch, "E293", {"start": v(820.67, -50.8) * mm, "end": v(-820.67, -50.8) * mm, "construction": true});
            skLineSegment(sketch, "E294", {"start": v(-820.67, -50.8) * mm, "end": v(-820.67, -1016) * mm, "construction": true});
            skLineSegment(sketch, "E295", {"start": v(-820.67, -986.53) * mm, "end": v(770.57, -50.8) * mm});
            skLineSegment(sketch, "E296", {"start": v(770.57, -50.8) * mm, "end": v(820.67, -50.8) * mm});
            skLineSegment(sketch, "E297", {"start": v(820.67, -80.27) * mm, "end": v(-770.57, -1016) * mm});
            skLineSegment(sketch, "E298", {"start": v(-770.57, -1016) * mm, "end": v(-820.67, -1016) * mm});
            skLineSegment(sketch, "E299", {"start": v(-820.67, -986.53) * mm, "end": v(-820.67, -1016) * mm});
            skLineSegment(sketch, "E300", {"start": v(820.67, -50.8) * mm, "end": v(820.67, -80.27) * mm});
            skLineSegment(sketch, "E301", {"start": v(820.67, -50.8) * mm, "end": v(770.57, -50.8) * mm});
            skSolve(sketch);
        }
        {
            var Q0;
            Q0 = qSketchRegion(id + "F76", true);
            extrude(context, id + "F77", {"entities" : qUnion([Q0]), "depth" : 25.4 * mm, "offsetDistance" : 25.4 * mm});
        }
        {
            var Q0;
            Q0=makeQuery(id+"F53.opExtrude","SWEPT_FACE",FACE,{"disambiguationData":[OSD([sQuery(id+"F52.wireOp",EDGE,"E152.right")])]});
            var sketch = newSketch(context, id + "F78", { "sketchPlane" : qUnion([Q0])});
            skPoint(sketch, "E302.0", {"position": v(-820.67, -50.8) * mm});
            skPoint(sketch, "E303.0", {"position": v(820.67, -1016) * mm});
            skLineSegment(sketch, "E304.0", {"start": v(820.67, -80.27) * mm, "end": v(-770.57, -1016) * mm, "construction": true});
            skLineSegment(sketch, "E305.0", {"start": v(-820.67, -986.53) * mm, "end": v(770.57, -50.8) * mm, "construction": true});
            skLineSegment(sketch, "E306", {"start": v(820.67, -1016) * mm, "end": v(-820.67, -50.8) * mm, "construction": true});
            skLineSegment(sketch, "E307", {"start": v(-820.67, -50.8) * mm, "end": v(-770.57, -50.8) * mm});
            skLineSegment(sketch, "E308", {"start": v(-770.57, -50.8) * mm, "end": v(0, -503.93) * mm});
            skLineSegment(sketch, "E309", {"start": v(820.67, -986.53) * mm, "end": v(820.67, -1016) * mm});
            skLineSegment(sketch, "E310", {"start": v(770.57, -1016) * mm, "end": v(820.67, -1016) * mm});
            skLineSegment(sketch, "E311", {"start": v(770.57, -1016) * mm, "end": v(0, -562.87) * mm});
            skLineSegment(sketch, "E312", {"start": v(-820.67, -80.27) * mm, "end": v(-820.67, -50.8) * mm});
            skLineSegment(sketch, "E313", {"start": v(-770.57, -50.8) * mm, "end": v(-820.67, -50.8) * mm});
            skLineSegment(sketch, "E314", {"start": v(-820.67, -50.8) * mm, "end": v(-820.67, -80.27) * mm});
            skLineSegment(sketch, "E315", {"start": v(0, -503.93) * mm, "end": v(-50.1, -533.4) * mm});
            skLineSegment(sketch, "E316", {"start": v(-50.1, -533.4) * mm, "end": v(0, -503.93) * mm});
            skLineSegment(sketch, "E317", {"start": v(0, -562.87) * mm, "end": v(50.1, -533.4) * mm});
            skLineSegment(sketch, "E318", {"start": v(50.1, -533.4) * mm, "end": v(0, -562.87) * mm});
            skLineSegment(sketch, "E319.trimOffspring", {"start": v(50.1, -533.4) * mm, "end": v(820.67, -986.53) * mm});
            skLineSegment(sketch, "E320.trimOffspring", {"start": v(-50.1, -533.4) * mm, "end": v(-820.67, -80.27) * mm});
            skSolve(sketch);
        }
        {
            var Q0;
            Q0 = qSketchRegion(id + "F78", true);
            extrude(context, id + "F79", {"entities" : qUnion([Q0]), "depth" : 25.4 * mm, "offsetDistance" : 25.4 * mm});
        }
    });
